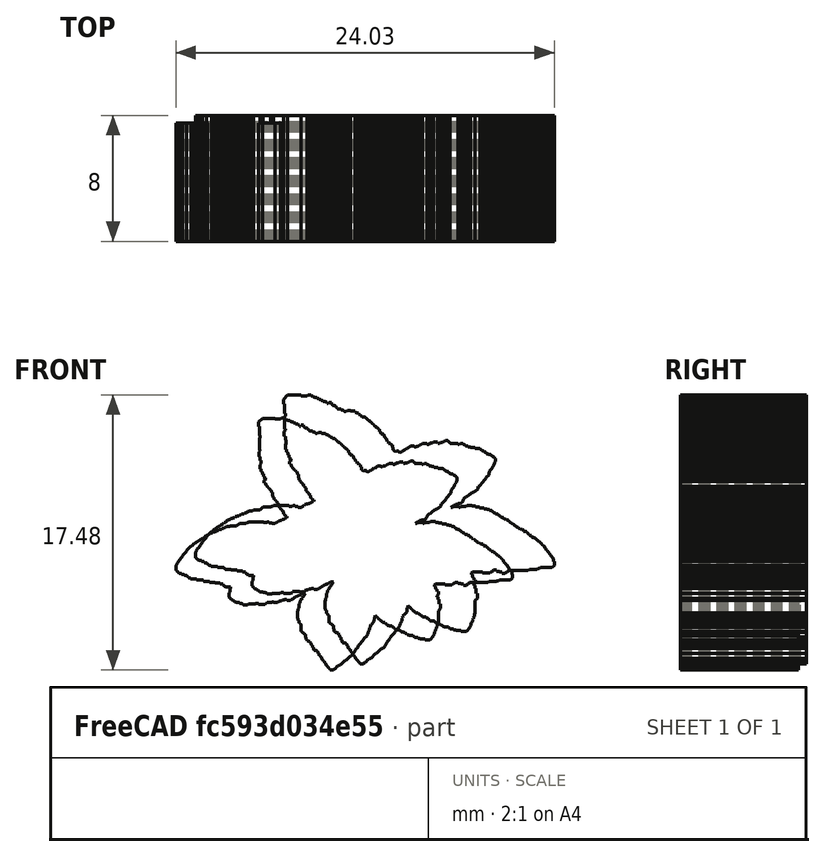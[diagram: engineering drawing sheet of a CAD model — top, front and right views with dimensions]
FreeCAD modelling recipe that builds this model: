
FCSTD DOCUMENT  (FreeCAD 0.20R29410 (Git))
Label: mintsLeafLogo_01_13_2023
License: All rights reserved
LicenseURL: http://en.wikipedia.org/wiki/All_rights_reserved
objects: Part::FeaturePython×2, Sketcher::SketchObject×1, Mesh::Feature×1, Part::Extrusion×1
note: 4 computed .brp shape members not serialized (recipe doc carries the construction recipe); baked Part::Feature solids carry a one-line shape summary decoded from their .brp

FEATURE [Sketcher::SketchObject] Sketch013
  FullyConstrained = false
  Placement = pos=(0,0,0) rot=(1,0,0;1.5708rad)
  sketch-geometry (884):
    g0: LineSegment StartX=35.7189 StartY=14.4677 StartZ=0 EndX=35.5415 EndY=14.2824 EndZ=0
    g1: LineSegment StartX=35.5415 StartY=14.2079 StartZ=0 EndX=35.4533 EndY=14.1342 EndZ=0
    g2: LineSegment StartX=35.4533 StartY=14.1342 StartZ=0 EndX=35.4583 EndY=14.0618 EndZ=0
    g3: LineSegment StartX=35.4583 StartY=14.0618 StartZ=0 EndX=35.3195 EndY=13.9216 EndZ=0
    g4: LineSegment StartX=35.3195 StartY=13.9216 StartZ=0 EndX=35.3195 EndY=13.853 EndZ=0
    g5: LineSegment StartX=35.3195 StartY=13.853 StartZ=0 EndX=35.248 EndY=13.7975 EndZ=0
    g6: LineSegment StartX=35.248 StartY=13.7975 StartZ=0 EndX=35.248 EndY=13.6573 EndZ=0
    g7: LineSegment StartX=35.248 StartY=13.6573 StartZ=0 EndX=35.1825 EndY=13.5912 EndZ=0
    g8: LineSegment StartX=35.1825 StartY=13.5912 StartZ=0 EndX=35.1825 EndY=13.2647 EndZ=0
    g9: LineSegment StartX=35.1825 StartY=13.2647 StartZ=0 EndX=35.0994 EndY=13.159 EndZ=0
    g10: LineSegment StartX=35.0994 StartY=13.159 StartZ=0 EndX=35.0994 EndY=13.0459 EndZ=0
    g11: LineSegment StartX=35.0994 StartY=13.0459 StartZ=0 EndX=35.0336 EndY=12.9565 EndZ=0
    g12: LineSegment StartX=35.0336 StartY=12.9565 StartZ=0 EndX=35.0336 EndY=12.3489 EndZ=0
    g13: LineSegment StartX=35.0336 StartY=12.3489 StartZ=0 EndX=35.1008 EndY=12.3489 EndZ=0
    g14: LineSegment StartX=35.1008 StartY=12.3489 StartZ=0 EndX=35.1008 EndY=12.2102 EndZ=0
    g15: LineSegment StartX=35.1008 StartY=12.2102 StartZ=0 EndX=35.1709 EndY=12.2072 EndZ=0
    g16: LineSegment StartX=35.1709 StartY=12.2072 StartZ=0 EndX=35.1709 EndY=11.9948 EndZ=0
    g17: LineSegment StartX=35.1709 StartY=11.9948 StartZ=0 EndX=35.2359 EndY=11.9948 EndZ=0
    g18: LineSegment StartX=35.2359 StartY=11.9948 StartZ=0 EndX=35.2359 EndY=11.9181 EndZ=0
    g19: LineSegment StartX=35.2359 StartY=11.9181 StartZ=0 EndX=35.3001 EndY=11.9181 EndZ=0
    g20: LineSegment StartX=35.3001 StartY=11.9181 StartZ=0 EndX=35.3001 EndY=11.8402 EndZ=0
    g21: LineSegment StartX=35.3001 StartY=11.8402 StartZ=0 EndX=35.3675 EndY=11.8402 EndZ=0
    g22: LineSegment StartX=35.3675 StartY=11.8402 StartZ=0 EndX=35.3675 EndY=11.2433 EndZ=0
    g23: LineSegment StartX=35.3675 StartY=11.2433 StartZ=0 EndX=35.435 EndY=11.2433 EndZ=0
    g24: LineSegment StartX=35.435 StartY=11.2433 StartZ=0 EndX=35.435 EndY=11.1727 EndZ=0
    g25: LineSegment StartX=35.435 StartY=11.1727 StartZ=0 EndX=35.5098 EndY=11.1727 EndZ=0
    g26: LineSegment StartX=35.5098 StartY=11.1727 StartZ=0 EndX=35.5098 EndY=11.1026 EndZ=0
    g27: LineSegment StartX=35.5098 StartY=11.1026 StartZ=0 EndX=35.6558 EndY=11.1026 EndZ=0
    g28: LineSegment StartX=35.6558 StartY=11.1026 StartZ=0 EndX=35.6558 EndY=11.0252 EndZ=0
    g29: LineSegment StartX=35.6558 StartY=11.0252 StartZ=0 EndX=35.7128 EndY=11.0252 EndZ=0
    g30: LineSegment StartX=35.7128 StartY=11.0252 StartZ=0 EndX=35.7128 EndY=10.7682 EndZ=0
    g31: LineSegment StartX=35.7128 StartY=10.7682 StartZ=0 EndX=35.7756 EndY=10.7681 EndZ=0
    g32: LineSegment StartX=35.7756 StartY=10.7681 StartZ=0 EndX=35.7756 EndY=10.5644 EndZ=0
    g33: LineSegment StartX=35.7756 StartY=10.5644 StartZ=0 EndX=35.846 EndY=10.5644 EndZ=0
    g34: LineSegment StartX=35.846 StartY=10.5644 StartZ=0 EndX=35.846 EndY=10.4767 EndZ=0
    g35: LineSegment StartX=35.846 StartY=10.4767 StartZ=0 EndX=35.988 EndY=10.4767 EndZ=0
    g36: LineSegment StartX=35.988 StartY=10.4767 StartZ=0 EndX=35.988 EndY=10.4228 EndZ=0
    g37: LineSegment StartX=35.988 StartY=10.4228 StartZ=0 EndX=36.1201 EndY=10.4228 EndZ=0
    g38: LineSegment StartX=36.1201 StartY=10.4228 StartZ=0 EndX=36.1201 EndY=10.2907 EndZ=0
    g39: LineSegment StartX=36.1201 StartY=10.2907 StartZ=0 EndX=36.1926 EndY=10.2907 EndZ=0
    g40: LineSegment StartX=36.1926 StartY=10.2907 StartZ=0 EndX=36.1926 EndY=10.1585 EndZ=0
    g41: LineSegment StartX=36.1926 StartY=10.1585 StartZ=0 EndX=36.2533 EndY=10.1585 EndZ=0
    g42: LineSegment StartX=36.2533 StartY=10.1585 StartZ=0 EndX=36.2533 EndY=10.0897 EndZ=0
    g43: LineSegment StartX=36.2533 StartY=10.0897 StartZ=0 EndX=36.3179 EndY=10.0897 EndZ=0
    g44: LineSegment StartX=36.3179 StartY=10.0897 StartZ=0 EndX=36.3179 EndY=9.8871 EndZ=0
    g45: LineSegment StartX=36.3179 StartY=9.8871 StartZ=0 EndX=36.3888 EndY=9.8871 EndZ=0
    g46: LineSegment StartX=36.3888 StartY=9.8871 StartZ=0 EndX=36.3888 EndY=9.73503 EndZ=0
    g47: LineSegment StartX=36.3888 StartY=9.73503 StartZ=0 EndX=36.4516 EndY=9.73503 EndZ=0
    g48: LineSegment StartX=36.4516 StartY=9.73503 StartZ=0 EndX=36.4516 EndY=9.65617 EndZ=0
    g49: LineSegment StartX=36.4516 StartY=9.65617 StartZ=0 EndX=36.6707 EndY=9.65617 EndZ=0
    g50: LineSegment StartX=36.6707 StartY=9.65617 StartZ=0 EndX=36.6707 EndY=9.58899 EndZ=0
    g51: LineSegment StartX=36.6707 StartY=9.58899 StartZ=0 EndX=36.7335 EndY=9.58899 EndZ=0
    g52: LineSegment StartX=36.7335 StartY=9.58899 StartZ=0 EndX=36.7335 EndY=9.51158 EndZ=0
    g53: LineSegment StartX=36.7335 StartY=9.51158 StartZ=0 EndX=36.7948 EndY=9.51158 EndZ=0
    g54: LineSegment StartX=36.7948 StartY=9.51158 StartZ=0 EndX=36.7948 EndY=9.40351 EndZ=0
    g55: LineSegment StartX=36.7948 StartY=9.40351 StartZ=0 EndX=36.8664 EndY=9.40351 EndZ=0
    g56: LineSegment StartX=36.8664 StartY=9.40351 StartZ=0 EndX=36.8664 EndY=9.2487 EndZ=0
    g57: LineSegment StartX=36.8664 StartY=9.2487 StartZ=0 EndX=36.9292 EndY=9.2487 EndZ=0
    g58: LineSegment StartX=36.9292 StartY=9.2487 StartZ=0 EndX=36.9292 EndY=9.18298 EndZ=0
    g59: LineSegment StartX=36.9292 StartY=9.18298 StartZ=0 EndX=37.0036 EndY=9.18298 EndZ=0
    g60: LineSegment StartX=37.0036 StartY=9.18298 StartZ=0 EndX=37.0036 EndY=9.12121 EndZ=0
    g61: LineSegment StartX=37.0036 StartY=9.12121 StartZ=0 EndX=37.066 EndY=9.12121 EndZ=0
    g62: LineSegment StartX=37.066 StartY=9.12121 StartZ=0 EndX=37.066 EndY=8.98122 EndZ=0
    g63: LineSegment StartX=37.066 StartY=8.98122 StartZ=0 EndX=37.1365 EndY=8.98122 EndZ=0
    g64: LineSegment StartX=37.1365 StartY=8.98122 StartZ=0 EndX=37.1365 EndY=8.85617 EndZ=0
    g65: LineSegment StartX=37.1365 StartY=8.85617 StartZ=0 EndX=37.2117 EndY=8.85617 EndZ=0
    g66: LineSegment StartX=37.2117 StartY=8.85617 StartZ=0 EndX=37.2117 EndY=8.77808 EndZ=0
    g67: LineSegment StartX=37.2117 StartY=8.77808 StartZ=0 EndX=37.276 EndY=8.7779 EndZ=0
    g68: LineSegment StartX=37.276 StartY=8.7779 StartZ=0 EndX=37.276 EndY=8.70839 EndZ=0
    g69: LineSegment StartX=37.276 StartY=8.70839 StartZ=0 EndX=37.3475 EndY=8.70839 EndZ=0
    g70: LineSegment StartX=37.3475 StartY=8.70839 StartZ=0 EndX=37.3475 EndY=8.58602 EndZ=0
    g71: LineSegment StartX=37.3475 StartY=8.58602 StartZ=0 EndX=37.4111 EndY=8.58602 EndZ=0
    g72: LineSegment StartX=37.4111 StartY=8.58602 StartZ=0 EndX=37.4111 EndY=8.50272 EndZ=0
    g73: LineSegment StartX=37.4111 StartY=8.50272 StartZ=0 EndX=37.4778 EndY=8.50272 EndZ=0
    g74: LineSegment StartX=37.4778 StartY=8.50272 StartZ=0 EndX=37.4778 EndY=8.37852 EndZ=0
    g75: LineSegment StartX=37.4778 StartY=8.37852 StartZ=0 EndX=37.55 EndY=8.37852 EndZ=0
    g76: LineSegment StartX=37.55 StartY=8.37852 StartZ=0 EndX=37.55 EndY=8.29594 EndZ=0
    g77: LineSegment StartX=37.55 StartY=8.29594 StartZ=0 EndX=37.6238 EndY=8.29594 EndZ=0
    g78: LineSegment StartX=37.6238 StartY=8.29594 StartZ=0 EndX=37.6238 EndY=8.20831 EndZ=0
    g79: LineSegment StartX=37.6238 StartY=8.20831 StartZ=0 EndX=37.6953 EndY=8.21123 EndZ=0
    g80: LineSegment StartX=37.6953 StartY=8.21123 StartZ=0 EndX=37.6953 EndY=8.14022 EndZ=0
    g81: LineSegment StartX=37.6953 StartY=8.14022 StartZ=0 EndX=37.7536 EndY=8.14414 EndZ=0
    g82: LineSegment StartX=37.7536 StartY=8.14414 StartZ=0 EndX=37.7574 EndY=8.06459 EndZ=0
    g83: LineSegment StartX=37.7574 StartY=8.06459 StartZ=0 EndX=37.8181 EndY=8.06459 EndZ=0
    g84: LineSegment StartX=37.8181 StartY=8.06459 StartZ=0 EndX=37.8216 EndY=7.98967 EndZ=0
    g85: LineSegment StartX=37.8216 StartY=7.98967 StartZ=0 EndX=38.1025 EndY=7.98967 EndZ=0
    g86: LineSegment StartX=38.1025 StartY=7.98967 StartZ=0 EndX=38.1917 EndY=8.08042 EndZ=0
    g87: LineSegment StartX=38.1917 StartY=8.08042 StartZ=0 EndX=38.2417 EndY=8.08577 EndZ=0
    g88: LineSegment StartX=38.2417 StartY=8.08577 StartZ=0 EndX=38.4557 EndY=8.32302 EndZ=0
    g89: LineSegment StartX=38.4557 StartY=8.32302 StartZ=0 EndX=38.5235 EndY=8.32302 EndZ=0
    g90: LineSegment StartX=38.5235 StartY=8.32302 StartZ=0 EndX=38.5887 EndY=8.40314 EndZ=0
    g91: LineSegment StartX=38.5887 StartY=8.40314 StartZ=0 EndX=38.6773 EndY=8.40314 EndZ=0
    g92: LineSegment StartX=38.6773 StartY=8.40314 StartZ=0 EndX=39.0643 EndY=8.80818 EndZ=0
    g93: LineSegment StartX=39.0643 StartY=8.80818 StartZ=0 EndX=39.152 EndY=8.80818 EndZ=0
    g94: LineSegment StartX=39.152 StartY=8.80818 StartZ=0 EndX=39.5355 EndY=9.19803 EndZ=0
    g95: LineSegment StartX=39.5355 StartY=9.19803 StartZ=0 EndX=39.6318 EndY=9.19803 EndZ=0
    g96: LineSegment StartX=39.6318 StartY=9.19803 StartZ=0 EndX=39.792 EndY=9.38195 EndZ=0
    g97: LineSegment StartX=39.792 StartY=9.38195 StartZ=0 EndX=39.7884 EndY=9.45608 EndZ=0
    g98: LineSegment StartX=39.7884 StartY=9.45608 StartZ=0 EndX=39.9772 EndY=9.63446 EndZ=0
    g99: LineSegment StartX=39.9772 StartY=9.63446 StartZ=0 EndX=39.9772 EndY=9.72533 EndZ=0
    g100: LineSegment StartX=39.9772 StartY=9.72533 StartZ=0 EndX=40.1697 EndY=9.91904 EndZ=0
    g101: LineSegment StartX=40.1697 StartY=9.91904 StartZ=0 EndX=40.1746 EndY=9.99558 EndZ=0
    g102: LineSegment StartX=40.1746 StartY=9.99558 StartZ=0 EndX=40.2388 EndY=10.0603 EndZ=0
    g103: LineSegment StartX=40.2388 StartY=10.0603 StartZ=0 EndX=40.2423 EndY=10.1261 EndZ=0
    g104: LineSegment StartX=40.2423 StartY=10.1261 StartZ=0 EndX=40.5948 EndY=10.4793 EndZ=0
    g105: LineSegment StartX=40.5948 StartY=10.4793 StartZ=0 EndX=40.5948 EndY=10.5499 EndZ=0
    g106: LineSegment StartX=40.5948 StartY=10.5499 StartZ=0 EndX=40.6701 EndY=10.618 EndZ=0
    g107: LineSegment StartX=40.6701 StartY=10.618 StartZ=0 EndX=40.6581 EndY=10.6527 EndZ=0
    g108: LineSegment StartX=40.6581 StartY=10.6527 StartZ=0 EndX=40.6988 EndY=10.6527 EndZ=0
    g109: LineSegment StartX=40.6988 StartY=10.6527 StartZ=0 EndX=40.9317 EndY=10.8877 EndZ=0
    g110: LineSegment StartX=40.9317 StartY=10.8877 StartZ=0 EndX=40.9317 EndY=10.9592 EndZ=0
    g111: LineSegment StartX=40.9317 StartY=10.9592 StartZ=0 EndX=41.0136 EndY=11.0405 EndZ=0
    g112: LineSegment StartX=41.0136 StartY=11.0405 StartZ=0 EndX=41.0068 EndY=11.1648 EndZ=0
    g113: LineSegment StartX=41.0068 StartY=11.1648 StartZ=0 EndX=41.0763 EndY=11.2275 EndZ=0
    g114: LineSegment StartX=41.0763 StartY=11.2275 StartZ=0 EndX=41.0723 EndY=11.2979 EndZ=0
    g115: LineSegment StartX=41.0723 StartY=11.2979 StartZ=0 EndX=41.15 EndY=11.3821 EndZ=0
    g116: LineSegment StartX=41.15 StartY=11.3821 StartZ=0 EndX=41.15 EndY=11.5724 EndZ=0
    g117: LineSegment StartX=41.15 StartY=11.5724 StartZ=0 EndX=41.2317 EndY=11.6351 EndZ=0
    g118: LineSegment StartX=41.2317 StartY=11.6351 StartZ=0 EndX=41.2155 EndY=11.7717 EndZ=0
    g119: LineSegment StartX=41.2155 StartY=11.7717 StartZ=0 EndX=41.2837 EndY=11.8432 EndZ=0
    g120: LineSegment StartX=41.2837 StartY=11.8432 StartZ=0 EndX=41.2786 EndY=11.8698 EndZ=0
    g121: LineSegment StartX=41.2786 StartY=11.8698 StartZ=0 EndX=41.3138 EndY=11.8698 EndZ=0
    g122: LineSegment StartX=41.3138 StartY=11.8698 StartZ=0 EndX=41.5455 EndY=12.1045 EndZ=0
    g123: LineSegment StartX=41.5455 StartY=12.1045 StartZ=0 EndX=41.5618 EndY=12.4305 EndZ=0
    g124: LineSegment StartX=41.5618 StartY=12.4305 StartZ=0 EndX=41.6277 EndY=12.505 EndZ=0
    g125: LineSegment StartX=41.6277 StartY=12.505 StartZ=0 EndX=41.6277 EndY=12.6108 EndZ=0
    g126: LineSegment StartX=41.6277 StartY=12.6108 StartZ=0 EndX=41.692 EndY=12.5393 EndZ=0
    g127: LineSegment StartX=41.692 StartY=12.5393 StartZ=0 EndX=41.7679 EndY=12.5393 EndZ=0
    g128: LineSegment StartX=41.7679 StartY=12.5393 StartZ=0 EndX=41.7679 EndY=12.4516 EndZ=0
    g129: LineSegment StartX=41.7679 StartY=12.4516 StartZ=0 EndX=41.8336 EndY=12.4546 EndZ=0
    g130: LineSegment StartX=41.8336 StartY=12.4546 StartZ=0 EndX=41.8336 EndY=12.3903 EndZ=0
    g131: LineSegment StartX=41.8336 StartY=12.3903 StartZ=0 EndX=41.8935 EndY=12.3903 EndZ=0
    g132: LineSegment StartX=41.8935 StartY=12.3903 StartZ=0 EndX=41.8935 EndY=12.3173 EndZ=0
    g133: LineSegment StartX=41.8935 StartY=12.3173 StartZ=0 EndX=41.9592 EndY=12.3217 EndZ=0
    g134: LineSegment StartX=41.9592 StartY=12.3217 StartZ=0 EndX=41.9651 EndY=12.2501 EndZ=0
    g135: LineSegment StartX=41.9651 StartY=12.2501 StartZ=0 EndX=42.0235 EndY=12.2559 EndZ=0
    g136: LineSegment StartX=42.0235 StartY=12.2559 StartZ=0 EndX=42.0264 EndY=12.1829 EndZ=0
    g137: LineSegment StartX=42.0264 StartY=12.1829 StartZ=0 EndX=42.1067 EndY=12.1888 EndZ=0
    g138: LineSegment StartX=42.1067 StartY=12.1888 StartZ=0 EndX=42.1067 EndY=12.1143 EndZ=0
    g139: LineSegment StartX=42.1067 StartY=12.1143 StartZ=0 EndX=42.2426 EndY=12.1216 EndZ=0
    g140: LineSegment StartX=42.2426 StartY=12.1216 StartZ=0 EndX=42.2426 EndY=12.0413 EndZ=0
    g141: LineSegment StartX=42.2426 StartY=12.0413 StartZ=0 EndX=42.4427 EndY=12.0413 EndZ=0
    g142: LineSegment StartX=42.4427 StartY=12.0413 StartZ=0 EndX=42.45 EndY=11.9566 EndZ=0
    g143: LineSegment StartX=42.45 StartY=11.9566 StartZ=0 EndX=42.523 EndY=11.9639 EndZ=0
    g144: LineSegment StartX=42.523 StartY=11.9639 StartZ=0 EndX=42.5274 EndY=11.8952 EndZ=0
    g145: LineSegment StartX=42.5274 StartY=11.8952 StartZ=0 EndX=42.5931 EndY=11.9011 EndZ=0
    g146: LineSegment StartX=42.5931 StartY=11.9011 StartZ=0 EndX=42.5931 EndY=11.847 EndZ=0
    g147: LineSegment StartX=42.5931 StartY=11.847 StartZ=0 EndX=42.6457 EndY=11.8499 EndZ=0
    g148: LineSegment StartX=42.6457 StartY=11.8499 StartZ=0 EndX=42.6457 EndY=11.7886 EndZ=0
    g149: LineSegment StartX=42.6457 StartY=11.7886 StartZ=0 EndX=42.7844 EndY=11.7886 EndZ=0
    g150: LineSegment StartX=42.7844 StartY=11.7886 StartZ=0 EndX=42.7844 EndY=11.7131 EndZ=0
    g151: LineSegment StartX=42.7844 StartY=11.7131 StartZ=0 EndX=43.0642 EndY=11.7131 EndZ=0
    g152: LineSegment StartX=43.0642 StartY=11.7131 StartZ=0 EndX=43.0642 EndY=11.6357 EndZ=0
    g153: LineSegment StartX=43.0642 StartY=11.6357 StartZ=0 EndX=43.1985 EndY=11.6357 EndZ=0
    g154: LineSegment StartX=43.1985 StartY=11.6357 StartZ=0 EndX=43.1985 EndY=11.5714 EndZ=0
    g155: LineSegment StartX=43.1985 StartY=11.5714 StartZ=0 EndX=43.2613 EndY=11.5714 EndZ=0
    g156: LineSegment StartX=43.2613 StartY=11.5714 StartZ=0 EndX=43.2613 EndY=11.5086 EndZ=0
    g157: LineSegment StartX=43.2613 StartY=11.5086 StartZ=0 EndX=43.3285 EndY=11.5086 EndZ=0
    g158: LineSegment StartX=43.3285 StartY=11.5086 StartZ=0 EndX=43.3285 EndY=11.4327 EndZ=0
    g159: LineSegment StartX=43.3285 StartY=11.4327 StartZ=0 EndX=43.3913 EndY=11.4371 EndZ=0
    g160: LineSegment StartX=43.3913 StartY=11.4371 StartZ=0 EndX=43.3932 EndY=11.3717 EndZ=0
    g161: LineSegment StartX=43.3932 StartY=11.3717 StartZ=0 EndX=43.7436 EndY=11.3717 EndZ=0
    g162: LineSegment StartX=43.7436 StartY=11.3717 StartZ=0 EndX=43.7436 EndY=11.3021 EndZ=0
    g163: LineSegment StartX=43.7436 StartY=11.3021 StartZ=0 EndX=43.8098 EndY=11.3021 EndZ=0
    g164: LineSegment StartX=43.8098 StartY=11.3021 StartZ=0 EndX=43.8134 EndY=11.2285 EndZ=0
    g165: LineSegment StartX=43.8134 StartY=11.2285 StartZ=0 EndX=44.0238 EndY=11.2285 EndZ=0
    g166: LineSegment StartX=44.0238 StartY=11.2285 StartZ=0 EndX=44.0238 EndY=11.1603 EndZ=0
    g167: LineSegment StartX=44.0238 StartY=11.1603 StartZ=0 EndX=44.1542 EndY=11.1603 EndZ=0
    g168: LineSegment StartX=44.1542 StartY=11.1603 StartZ=0 EndX=44.1506 EndY=11.0922 EndZ=0
    g169: LineSegment StartX=44.1506 StartY=11.0922 StartZ=0 EndX=44.2845 EndY=11.1005 EndZ=0
    g170: LineSegment StartX=44.2845 StartY=11.1005 StartZ=0 EndX=44.2845 EndY=11.0276 EndZ=0
    g171: LineSegment StartX=44.2845 StartY=11.0276 StartZ=0 EndX=44.3538 EndY=11.0312 EndZ=0
    g172: LineSegment StartX=44.3538 StartY=11.0312 StartZ=0 EndX=44.3538 EndY=10.9534 EndZ=0
    g173: LineSegment StartX=44.3538 StartY=10.9534 StartZ=0 EndX=44.4925 EndY=10.9534 EndZ=0
    g174: LineSegment StartX=44.4925 StartY=10.9534 StartZ=0 EndX=44.4925 EndY=10.9066 EndZ=0
    g175: LineSegment StartX=44.4925 StartY=10.9066 StartZ=0 EndX=44.8405 EndY=10.9066 EndZ=0
    g176: LineSegment StartX=44.8405 StartY=10.9066 StartZ=0 EndX=44.8405 EndY=10.8227 EndZ=0
    g177: LineSegment StartX=44.8405 StartY=10.8227 StartZ=0 EndX=44.9671 EndY=10.8245 EndZ=0
    g178: LineSegment StartX=44.9671 StartY=10.8245 StartZ=0 EndX=44.9671 EndY=10.7496 EndZ=0
    g179: LineSegment StartX=44.9671 StartY=10.7496 StartZ=0 EndX=45.2382 EndY=10.7496 EndZ=0
    g180: LineSegment StartX=45.2382 StartY=10.7496 StartZ=0 EndX=45.2382 EndY=10.6783 EndZ=0
    g181: LineSegment StartX=45.2382 StartY=10.6783 StartZ=0 EndX=45.438 EndY=10.6783 EndZ=0
    g182: LineSegment StartX=45.438 StartY=10.6783 StartZ=0 EndX=45.438 EndY=10.6176 EndZ=0
    g183: LineSegment StartX=45.438 StartY=10.6176 StartZ=0 EndX=45.8572 EndY=10.6176 EndZ=0
    g184: LineSegment StartX=45.8572 StartY=10.6176 StartZ=0 EndX=45.8572 EndY=10.548 EndZ=0
    g185: LineSegment StartX=45.8572 StartY=10.548 StartZ=0 EndX=46.2711 EndY=10.548 EndZ=0
    g186: LineSegment StartX=46.2711 StartY=10.548 StartZ=0 EndX=46.5712 EndY=10.876 EndZ=0
    g187: LineSegment StartX=46.5712 StartY=10.876 StartZ=0 EndX=46.568 EndY=10.9537 EndZ=0
    g188: LineSegment StartX=46.568 StartY=10.9537 StartZ=0 EndX=46.6513 EndY=11.0387 EndZ=0
    g189: LineSegment StartX=46.6513 StartY=11.0387 StartZ=0 EndX=46.6513 EndY=11.2162 EndZ=0
    g190: LineSegment StartX=46.6513 StartY=11.2162 StartZ=0 EndX=46.7535 EndY=11.317 EndZ=0
    g191: LineSegment StartX=46.7535 StartY=11.317 StartZ=0 EndX=46.7462 EndY=11.4353 EndZ=0
    g192: LineSegment StartX=46.7462 StartY=11.4353 StartZ=0 EndX=46.8178 EndY=11.5141 EndZ=0
    g193: LineSegment StartX=46.8178 StartY=11.5141 StartZ=0 EndX=46.8081 EndY=11.636 EndZ=0
    g194: LineSegment StartX=46.8081 StartY=11.636 StartZ=0 EndX=46.8919 EndY=11.7287 EndZ=0
    g195: LineSegment StartX=46.8919 StartY=11.7287 StartZ=0 EndX=46.8919 EndY=11.9142 EndZ=0
    g196: LineSegment StartX=46.8919 StartY=11.9142 StartZ=0 EndX=46.9704 EndY=12.0106 EndZ=0
    g197: LineSegment StartX=46.9704 StartY=12.0106 StartZ=0 EndX=46.9704 EndY=13.0147 EndZ=0
    g198: LineSegment StartX=46.9704 StartY=13.0147 StartZ=0 EndX=47.1435 EndY=13.1957 EndZ=0
    g199: LineSegment StartX=47.1435 StartY=13.1957 StartZ=0 EndX=47.1435 EndY=13.5812 EndZ=0
    g200: LineSegment StartX=47.1435 StartY=13.5812 StartZ=0 EndX=47.0232 EndY=13.5812 EndZ=0
    g201: LineSegment StartX=47.0232 StartY=13.5812 StartZ=0 EndX=47.0232 EndY=13.968 EndZ=0
    g202: LineSegment StartX=47.0232 StartY=13.968 StartZ=0 EndX=46.9387 EndY=13.981 EndZ=0
    g203: LineSegment StartX=46.9387 StartY=13.981 StartZ=0 EndX=46.9387 EndY=14.1923 EndZ=0
    g204: LineSegment StartX=46.9387 StartY=14.1923 StartZ=0 EndX=46.8607 EndY=14.189 EndZ=0
    g205: LineSegment StartX=46.8607 StartY=14.189 StartZ=0 EndX=46.8607 EndY=14.2768 EndZ=0
    g206: LineSegment StartX=46.8607 StartY=14.2768 StartZ=0 EndX=46.9745 EndY=14.4003 EndZ=0
    g207: LineSegment StartX=46.9745 StartY=14.4003 StartZ=0 EndX=46.9842 EndY=14.6473 EndZ=0
    g208: LineSegment StartX=46.9842 StartY=14.6473 StartZ=0 EndX=46.8672 EndY=14.6603 EndZ=0
    g209: LineSegment StartX=46.8672 StartY=14.6603 StartZ=0 EndX=46.8672 EndY=14.8066 EndZ=0
    g210: LineSegment StartX=46.8672 StartY=14.8066 StartZ=0 EndX=46.799 EndY=14.8131 EndZ=0
    g211: LineSegment StartX=46.799 StartY=14.8131 StartZ=0 EndX=46.7957 EndY=14.8846 EndZ=0
    g212: LineSegment StartX=46.7957 StartY=14.8846 StartZ=0 EndX=46.7372 EndY=14.8911 EndZ=0
    g213: LineSegment StartX=46.7372 StartY=14.8911 StartZ=0 EndX=46.7502 EndY=15.0699 EndZ=0
    g214: LineSegment StartX=46.7502 StartY=15.0699 StartZ=0 EndX=46.6592 EndY=15.0764 EndZ=0
    g215: LineSegment StartX=46.6592 StartY=15.0764 StartZ=0 EndX=46.6592 EndY=15.2096 EndZ=0
    g216: LineSegment StartX=46.6592 StartY=15.2096 StartZ=0 EndX=46.7535 EndY=15.2811 EndZ=0
    g217: LineSegment StartX=46.7535 StartY=15.2811 StartZ=0 EndX=47.5498 EndY=15.2811 EndZ=0
    g218: LineSegment StartX=47.5498 StartY=15.2811 StartZ=0 EndX=47.5498 EndY=15.2015 EndZ=0
    g219: LineSegment StartX=47.5498 StartY=15.2015 StartZ=0 EndX=48.1326 EndY=15.2015 EndZ=0
    g220: LineSegment StartX=48.1326 StartY=15.2015 StartZ=0 EndX=48.1915 EndY=15.2887 EndZ=0
    g221: LineSegment StartX=48.1915 StartY=15.2887 StartZ=0 EndX=48.2811 EndY=15.2887 EndZ=0
    g222: LineSegment StartX=48.2811 StartY=15.2887 StartZ=0 EndX=48.4046 EndY=15.4194 EndZ=0
    g223: LineSegment StartX=48.4046 StartY=15.4194 StartZ=0 EndX=48.6512 EndY=15.4194 EndZ=0
    g224: LineSegment StartX=48.6512 StartY=15.4194 StartZ=0 EndX=48.6512 EndY=15.3322 EndZ=0
    g225: LineSegment StartX=48.6512 StartY=15.3322 StartZ=0 EndX=48.9084 EndY=15.3322 EndZ=0
    g226: LineSegment StartX=48.9084 StartY=15.3322 StartZ=0 EndX=48.9084 EndY=15.2647 EndZ=0
    g227: LineSegment StartX=48.9084 StartY=15.2647 StartZ=0 EndX=49.1131 EndY=15.2647 EndZ=0
    g228: LineSegment StartX=49.1131 StartY=15.2647 StartZ=0 EndX=49.1131 EndY=15.171 EndZ=0
    g229: LineSegment StartX=49.1131 StartY=15.171 StartZ=0 EndX=49.344 EndY=15.171 EndZ=0
    g230: LineSegment StartX=49.344 StartY=15.171 StartZ=0 EndX=49.4317 EndY=15.2779 EndZ=0
    g231: LineSegment StartX=49.4317 StartY=15.2779 StartZ=0 EndX=49.513 EndY=15.2714 EndZ=0
    g232: LineSegment StartX=49.513 StartY=15.2714 StartZ=0 EndX=49.6365 EndY=15.4177 EndZ=0
    g233: LineSegment StartX=49.6365 StartY=15.4177 StartZ=0 EndX=51.1609 EndY=15.4177 EndZ=0
    g234: LineSegment StartX=51.1609 StartY=15.4177 StartZ=0 EndX=51.2713 EndY=15.4747 EndZ=0
    g235: LineSegment StartX=51.2713 StartY=15.4747 StartZ=0 EndX=51.8707 EndY=15.4747 EndZ=0
    g236: LineSegment StartX=51.8707 StartY=15.4747 StartZ=0 EndX=51.9501 EndY=15.5501 EndZ=0
    g237: LineSegment StartX=51.9501 StartY=15.5501 StartZ=0 EndX=52.0613 EndY=15.5501 EndZ=0
    g238: LineSegment StartX=52.0613 StartY=15.5501 StartZ=0 EndX=52.1566 EndY=15.6335 EndZ=0
    g239: LineSegment StartX=52.1566 StartY=15.6335 StartZ=0 EndX=53.0776 EndY=15.6335 EndZ=0
    g240: LineSegment StartX=53.0776 StartY=15.6335 StartZ=0 EndX=53.2557 EndY=15.8082 EndZ=0
    g241: LineSegment StartX=53.2557 StartY=15.8082 StartZ=0 EndX=53.2557 EndY=16.103 EndZ=0
    g242: LineSegment StartX=53.2557 StartY=16.103 StartZ=0 EndX=53.1958 EndY=16.103 EndZ=0
    g243: LineSegment StartX=53.1958 StartY=16.103 StartZ=0 EndX=53.1958 EndY=16.3046 EndZ=0
    g244: LineSegment StartX=53.1958 StartY=16.3046 StartZ=0 EndX=53.1301 EndY=16.3017 EndZ=0
    g245: LineSegment StartX=53.1301 StartY=16.3017 StartZ=0 EndX=53.1301 EndY=16.4404 EndZ=0
    g246: LineSegment StartX=53.1301 StartY=16.4404 StartZ=0 EndX=53.0594 EndY=16.4404 EndZ=0
    g247: LineSegment StartX=53.0594 StartY=16.4404 StartZ=0 EndX=53.0558 EndY=16.5171 EndZ=0
    g248: LineSegment StartX=53.0558 StartY=16.5171 StartZ=0 EndX=52.9773 EndY=16.5171 EndZ=0
    g249: LineSegment StartX=52.9773 StartY=16.5171 StartZ=0 EndX=52.9773 EndY=16.6455 EndZ=0
    g250: LineSegment StartX=52.9773 StartY=16.6455 StartZ=0 EndX=52.9219 EndY=16.6452 EndZ=0
    g251: LineSegment StartX=52.9219 StartY=16.6452 StartZ=0 EndX=52.9219 EndY=16.7146 EndZ=0
    g252: LineSegment StartX=52.9219 StartY=16.7146 StartZ=0 EndX=52.8549 EndY=16.7146 EndZ=0
    g253: LineSegment StartX=52.8549 StartY=16.7146 StartZ=0 EndX=52.8535 EndY=16.7863 EndZ=0
    g254: LineSegment StartX=52.8535 StartY=16.7863 StartZ=0 EndX=52.7868 EndY=16.7863 EndZ=0
    g255: LineSegment StartX=52.7868 StartY=16.7863 StartZ=0 EndX=52.7868 EndY=16.9211 EndZ=0
    g256: LineSegment StartX=52.7868 StartY=16.9211 StartZ=0 EndX=52.715 EndY=16.9211 EndZ=0
    g257: LineSegment StartX=52.715 StartY=16.9211 StartZ=0 EndX=52.715 EndY=16.98 EndZ=0
    g258: LineSegment StartX=52.715 StartY=16.98 StartZ=0 EndX=52.6457 EndY=16.98 EndZ=0
    g259: LineSegment StartX=52.6457 StartY=16.98 StartZ=0 EndX=52.6457 EndY=17.0366 EndZ=0
    g260: LineSegment StartX=52.6457 StartY=17.0366 StartZ=0 EndX=52.5763 EndY=17.0366 EndZ=0
    g261: LineSegment StartX=52.5763 StartY=17.0366 StartZ=0 EndX=52.5763 EndY=17.128 EndZ=0
    g262: LineSegment StartX=52.5763 StartY=17.128 StartZ=0 EndX=52.5147 EndY=17.128 EndZ=0
    g263: LineSegment StartX=52.5147 StartY=17.128 StartZ=0 EndX=52.5147 EndY=17.2695 EndZ=0
    g264: LineSegment StartX=52.5147 StartY=17.2695 StartZ=0 EndX=52.4502 EndY=17.2647 EndZ=0
    g265: LineSegment StartX=52.4502 StartY=17.2647 StartZ=0 EndX=52.4454 EndY=17.336 EndZ=0
    g266: LineSegment StartX=52.4454 StartY=17.336 StartZ=0 EndX=52.3797 EndY=17.3384 EndZ=0
    g267: LineSegment StartX=52.3797 StartY=17.3384 StartZ=0 EndX=52.3829 EndY=17.4058 EndZ=0
    g268: LineSegment StartX=52.3829 StartY=17.4058 StartZ=0 EndX=52.318 EndY=17.4026 EndZ=0
    g269: LineSegment StartX=52.318 StartY=17.4026 StartZ=0 EndX=52.318 EndY=17.4715 EndZ=0
    g270: LineSegment StartX=52.318 StartY=17.4715 StartZ=0 EndX=52.2451 EndY=17.4715 EndZ=0
    g271: LineSegment StartX=52.2451 StartY=17.4715 StartZ=0 EndX=52.2451 EndY=17.5364 EndZ=0
    g272: LineSegment StartX=52.2451 StartY=17.5364 StartZ=0 EndX=52.1833 EndY=17.5388 EndZ=0
    g273: LineSegment StartX=52.1833 StartY=17.5388 StartZ=0 EndX=52.1833 EndY=17.6077 EndZ=0
    g274: LineSegment StartX=52.1833 StartY=17.6077 StartZ=0 EndX=52.1144 EndY=17.6077 EndZ=0
    g275: LineSegment StartX=52.1144 StartY=17.6077 StartZ=0 EndX=52.1144 EndY=17.6741 EndZ=0
    g276: LineSegment StartX=52.1144 StartY=17.6741 StartZ=0 EndX=52.0495 EndY=17.6741 EndZ=0
    g277: LineSegment StartX=52.0495 StartY=17.6741 StartZ=0 EndX=52.0495 EndY=17.7495 EndZ=0
    g278: LineSegment StartX=52.0495 StartY=17.7495 StartZ=0 EndX=51.9017 EndY=17.7495 EndZ=0
    g279: LineSegment StartX=51.9017 StartY=17.7495 StartZ=0 EndX=51.9017 EndY=17.8092 EndZ=0
    g280: LineSegment StartX=51.9017 StartY=17.8092 StartZ=0 EndX=51.8351 EndY=17.8092 EndZ=0
    g281: LineSegment StartX=51.8351 StartY=17.8092 StartZ=0 EndX=51.8351 EndY=17.8911 EndZ=0
    g282: LineSegment StartX=51.8351 StartY=17.8911 StartZ=0 EndX=51.7639 EndY=17.8911 EndZ=0
    g283: LineSegment StartX=51.7639 StartY=17.8911 StartZ=0 EndX=51.7639 EndY=17.9626 EndZ=0
    g284: LineSegment StartX=51.7639 StartY=17.9626 StartZ=0 EndX=51.6325 EndY=17.9626 EndZ=0
    g285: LineSegment StartX=51.6325 StartY=17.9626 StartZ=0 EndX=51.6325 EndY=18.0284 EndZ=0
    g286: LineSegment StartX=51.6325 StartY=18.0284 StartZ=0 EndX=51.485 EndY=18.0284 EndZ=0
    g287: LineSegment StartX=51.485 StartY=18.0284 StartZ=0 EndX=51.485 EndY=18.0711 EndZ=0
    g288: LineSegment StartX=51.485 StartY=18.0711 StartZ=0 EndX=51.4163 EndY=18.0711 EndZ=0
    g289: LineSegment StartX=51.4163 StartY=18.0711 StartZ=0 EndX=51.4163 EndY=18.1587 EndZ=0
    g290: LineSegment StartX=51.4163 StartY=18.1587 StartZ=0 EndX=51.2878 EndY=18.1587 EndZ=0
    g291: LineSegment StartX=51.2878 StartY=18.1587 StartZ=0 EndX=51.2878 EndY=18.2275 EndZ=0
    g292: LineSegment StartX=51.2878 StartY=18.2275 StartZ=0 EndX=51.2232 EndY=18.2275 EndZ=0
    g293: LineSegment StartX=51.2232 StartY=18.2275 StartZ=0 EndX=51.2267 EndY=18.2921 EndZ=0
    g294: LineSegment StartX=51.2267 StartY=18.2921 StartZ=0 EndX=51.1526 EndY=18.2921 EndZ=0
    g295: LineSegment StartX=51.1526 StartY=18.2921 StartZ=0 EndX=51.1526 EndY=18.3662 EndZ=0
    g296: LineSegment StartX=51.1526 StartY=18.3662 StartZ=0 EndX=51.0845 EndY=18.3602 EndZ=0
    g297: LineSegment StartX=51.0845 StartY=18.3602 StartZ=0 EndX=51.0845 EndY=18.4424 EndZ=0
    g298: LineSegment StartX=51.0845 StartY=18.4424 StartZ=0 EndX=51.0222 EndY=18.4424 EndZ=0
    g299: LineSegment StartX=51.0222 StartY=18.4424 StartZ=0 EndX=51.0222 EndY=18.5138 EndZ=0
    g300: LineSegment StartX=51.0222 StartY=18.5138 StartZ=0 EndX=50.8169 EndY=18.5138 EndZ=0
    g301: LineSegment StartX=50.8169 StartY=18.5138 StartZ=0 EndX=50.7878 EndY=18.6026 EndZ=0
    g302: LineSegment StartX=50.7878 StartY=18.6026 StartZ=0 EndX=50.7494 EndY=18.6113 EndZ=0
    g303: LineSegment StartX=50.7494 StartY=18.6113 StartZ=0 EndX=50.7397 EndY=18.6731 EndZ=0
    g304: LineSegment StartX=50.7397 StartY=18.6731 StartZ=0 EndX=50.5414 EndY=18.6536 EndZ=0
    g305: LineSegment StartX=50.5414 StartY=18.6536 StartZ=0 EndX=50.5381 EndY=18.7381 EndZ=0
    g306: LineSegment StartX=50.5381 StartY=18.7381 StartZ=0 EndX=50.4114 EndY=18.7218 EndZ=0
    g307: LineSegment StartX=50.4114 StartY=18.7218 StartZ=0 EndX=50.3951 EndY=18.7934 EndZ=0
    g308: LineSegment StartX=50.3951 StartY=18.7934 StartZ=0 EndX=50.3334 EndY=18.7934 EndZ=0
    g309: LineSegment StartX=50.3334 StartY=18.7934 StartZ=0 EndX=50.3366 EndY=18.8389 EndZ=0
    g310: LineSegment StartX=50.3366 StartY=18.8389 StartZ=0 EndX=50.2066 EndY=18.8389 EndZ=0
    g311: LineSegment StartX=50.2066 StartY=18.8389 StartZ=0 EndX=50.2099 EndY=18.9201 EndZ=0
    g312: LineSegment StartX=50.2099 StartY=18.9201 StartZ=0 EndX=50.1254 EndY=18.9266 EndZ=0
    g313: LineSegment StartX=50.1254 StartY=18.9266 StartZ=0 EndX=50.1156 EndY=19.0046 EndZ=0
    g314: LineSegment StartX=50.1156 StartY=19.0046 StartZ=0 EndX=49.9986 EndY=18.9949 EndZ=0
    g315: LineSegment StartX=49.9986 StartY=18.9949 StartZ=0 EndX=49.9921 EndY=19.0859 EndZ=0
    g316: LineSegment StartX=49.9921 StartY=19.0859 StartZ=0 EndX=49.9368 EndY=19.0501 EndZ=0
    g317: LineSegment StartX=49.9368 StartY=19.0501 StartZ=0 EndX=49.9206 EndY=19.1509 EndZ=0
    g318: LineSegment StartX=49.9206 StartY=19.1509 StartZ=0 EndX=49.7971 EndY=19.1281 EndZ=0
    g319: LineSegment StartX=49.7971 StartY=19.1281 StartZ=0 EndX=49.8068 EndY=19.2029 EndZ=0
    g320: LineSegment StartX=49.8068 StartY=19.2029 StartZ=0 EndX=49.7288 EndY=19.1899 EndZ=0
    g321: LineSegment StartX=49.7288 StartY=19.1899 StartZ=0 EndX=49.7191 EndY=19.2582 EndZ=0
    g322: LineSegment StartX=49.7191 StartY=19.2582 StartZ=0 EndX=49.6606 EndY=19.2647 EndZ=0
    g323: LineSegment StartX=49.6606 StartY=19.2647 StartZ=0 EndX=49.6541 EndY=19.3329 EndZ=0
    g324: LineSegment StartX=49.6541 StartY=19.3329 StartZ=0 EndX=49.6021 EndY=19.3329 EndZ=0
    g325: LineSegment StartX=49.6021 StartY=19.3329 StartZ=0 EndX=49.5988 EndY=19.4077 EndZ=0
    g326: LineSegment StartX=49.5988 StartY=19.4077 StartZ=0 EndX=49.4623 EndY=19.3947 EndZ=0
    g327: LineSegment StartX=49.4623 StartY=19.3947 StartZ=0 EndX=49.4623 EndY=19.4727 EndZ=0
    g328: LineSegment StartX=49.4623 StartY=19.4727 StartZ=0 EndX=49.2543 EndY=19.4532 EndZ=0
    g329: LineSegment StartX=49.2543 StartY=19.4532 StartZ=0 EndX=49.2543 EndY=19.5279 EndZ=0
    g330: LineSegment StartX=49.2543 StartY=19.5279 StartZ=0 EndX=49.199 EndY=19.5279 EndZ=0
    g331: LineSegment StartX=49.199 StartY=19.5279 StartZ=0 EndX=49.199 EndY=19.6189 EndZ=0
    g332: LineSegment StartX=49.199 StartY=19.6189 StartZ=0 EndX=49.0658 EndY=19.6059 EndZ=0
    g333: LineSegment StartX=49.0658 StartY=19.6059 StartZ=0 EndX=49.0495 EndY=19.6612 EndZ=0
    g334: LineSegment StartX=49.0495 StartY=19.6612 StartZ=0 EndX=48.991 EndY=19.6547 EndZ=0
    g335: LineSegment StartX=48.991 StartY=19.6547 StartZ=0 EndX=48.9845 EndY=19.7359 EndZ=0
    g336: LineSegment StartX=48.9845 StartY=19.7359 StartZ=0 EndX=48.8577 EndY=19.7262 EndZ=0
    g337: LineSegment StartX=48.8577 StartY=19.7262 StartZ=0 EndX=48.8577 EndY=19.8149 EndZ=0
    g338: LineSegment StartX=48.8577 StartY=19.8149 StartZ=0 EndX=48.7743 EndY=19.8069 EndZ=0
    g339: LineSegment StartX=48.7743 StartY=19.8069 StartZ=0 EndX=48.7743 EndY=19.8894 EndZ=0
    g340: LineSegment StartX=48.7743 StartY=19.8894 StartZ=0 EndX=48.5854 EndY=19.8894 EndZ=0
    g341: LineSegment StartX=48.5854 StartY=19.8894 StartZ=0 EndX=48.5854 EndY=19.9533 EndZ=0
    g342: LineSegment StartX=48.5854 StartY=19.9533 StartZ=0 EndX=48.4417 EndY=19.9533 EndZ=0
    g343: LineSegment StartX=48.4417 StartY=19.9533 StartZ=0 EndX=48.4417 EndY=20.0118 EndZ=0
    g344: LineSegment StartX=48.4417 StartY=20.0118 StartZ=0 EndX=48.3751 EndY=20.0118 EndZ=0
    g345: LineSegment StartX=48.3751 StartY=20.0118 StartZ=0 EndX=48.3751 EndY=20.089 EndZ=0
    g346: LineSegment StartX=48.3751 StartY=20.089 StartZ=0 EndX=48.3033 EndY=20.089 EndZ=0
    g347: LineSegment StartX=48.3033 StartY=20.089 StartZ=0 EndX=48.3033 EndY=20.1524 EndZ=0
    g348: LineSegment StartX=48.3033 StartY=20.1524 StartZ=0 EndX=48.0916 EndY=20.1524 EndZ=0
    g349: LineSegment StartX=48.0916 StartY=20.1524 StartZ=0 EndX=48.0916 EndY=20.2331 EndZ=0
    g350: LineSegment StartX=48.0916 StartY=20.2331 StartZ=0 EndX=47.8912 EndY=20.2331 EndZ=0
    g351: LineSegment StartX=47.8912 StartY=20.2331 StartZ=0 EndX=47.8912 EndY=20.2962 EndZ=0
    g352: LineSegment StartX=47.8912 StartY=20.2962 StartZ=0 EndX=47.6864 EndY=20.2962 EndZ=0
    g353: LineSegment StartX=47.6864 StartY=20.2962 StartZ=0 EndX=47.6864 EndY=20.3681 EndZ=0
    g354: LineSegment StartX=47.6864 StartY=20.3681 StartZ=0 EndX=47.2898 EndY=20.3681 EndZ=0
    g355: LineSegment StartX=47.2898 StartY=20.3681 StartZ=0 EndX=47.2898 EndY=20.4313 EndZ=0
    g356: LineSegment StartX=47.2898 StartY=20.4313 StartZ=0 EndX=47.0094 EndY=20.4313 EndZ=0
    g357: LineSegment StartX=47.0094 StartY=20.4313 StartZ=0 EndX=47.0094 EndY=20.5033 EndZ=0
    g358: LineSegment StartX=47.0094 StartY=20.5033 StartZ=0 EndX=46.7265 EndY=20.5033 EndZ=0
    g359: LineSegment StartX=46.7265 StartY=20.5033 StartZ=0 EndX=46.7265 EndY=20.5623 EndZ=0
    g360: LineSegment StartX=46.7265 StartY=20.5623 StartZ=0 EndX=46.3195 EndY=20.5623 EndZ=0
    g361: LineSegment StartX=46.3195 StartY=20.5623 StartZ=0 EndX=46.2304 EndY=20.478 EndZ=0
    g362: LineSegment StartX=46.2304 StartY=20.478 StartZ=0 EndX=45.8403 EndY=20.478 EndZ=0
    g363: LineSegment StartX=45.8403 StartY=20.478 StartZ=0 EndX=45.7581 EndY=20.3987 EndZ=0
    g364: LineSegment StartX=45.7581 StartY=20.3987 StartZ=0 EndX=45.6847 EndY=20.3987 EndZ=0
    g365: LineSegment StartX=45.6847 StartY=20.3987 StartZ=0 EndX=45.6847 EndY=20.4757 EndZ=0
    g366: LineSegment StartX=45.6847 StartY=20.4757 StartZ=0 EndX=45.2353 EndY=20.4757 EndZ=0
    g367: LineSegment StartX=45.2353 StartY=20.4757 StartZ=0 EndX=45.1511 EndY=20.3964 EndZ=0
    g368: LineSegment StartX=45.1511 StartY=20.3964 StartZ=0 EndX=45.039 EndY=20.3905 EndZ=0
    g369: LineSegment StartX=45.1271 StartY=20.498 StartZ=0 EndX=45.039 EndY=20.3905 EndZ=0
    g370: LineSegment StartX=45.1271 StartY=20.498 StartZ=0 EndX=45.1672 EndY=20.498 EndZ=0
    g371: LineSegment StartX=45.1672 StartY=20.498 StartZ=0 EndX=45.2586 EndY=20.5605 EndZ=0
    g372: LineSegment StartX=45.2586 StartY=20.5605 StartZ=0 EndX=45.3242 EndY=20.5605 EndZ=0
    g373: LineSegment StartX=45.3242 StartY=20.5605 StartZ=0 EndX=45.4009 EndY=20.6461 EndZ=0
    g374: LineSegment StartX=45.4009 StartY=20.6461 StartZ=0 EndX=45.5221 EndY=20.6461 EndZ=0
    g375: LineSegment StartX=45.5221 StartY=20.6461 StartZ=0 EndX=45.6149 EndY=20.705 EndZ=0
    g376: LineSegment StartX=45.6149 StartY=20.705 StartZ=0 EndX=45.8042 EndY=20.705 EndZ=0
    g377: LineSegment StartX=45.8042 StartY=20.705 StartZ=0 EndX=45.9915 EndY=20.8898 EndZ=0
    g378: LineSegment StartX=45.9915 StartY=20.8898 StartZ=0 EndX=45.9915 EndY=20.959 EndZ=0
    g379: LineSegment StartX=45.9915 StartY=20.959 StartZ=0 EndX=46.0581 EndY=21.0202 EndZ=0
    g380: LineSegment StartX=46.0581 StartY=21.0202 StartZ=0 EndX=46.0527 EndY=21.0894 EndZ=0
    g381: LineSegment StartX=46.0527 StartY=21.0894 StartZ=0 EndX=46.2124 EndY=21.2464 EndZ=0
    g382: LineSegment StartX=46.2124 StartY=21.2464 StartZ=0 EndX=46.2763 EndY=21.2277 EndZ=0
    g383: LineSegment StartX=46.2763 StartY=21.2277 StartZ=0 EndX=46.5051 EndY=21.4486 EndZ=0
    g384: LineSegment StartX=46.5051 StartY=21.4486 StartZ=0 EndX=46.585 EndY=21.4539 EndZ=0
    g385: LineSegment StartX=46.585 StartY=21.4539 StartZ=0 EndX=46.6994 EndY=21.603 EndZ=0
    g386: LineSegment StartX=46.6994 StartY=21.603 StartZ=0 EndX=46.8245 EndY=21.5843 EndZ=0
    g387: LineSegment StartX=46.8245 StartY=21.5843 StartZ=0 EndX=46.9016 EndY=21.6855 EndZ=0
    g388: LineSegment StartX=46.9016 StartY=21.6855 StartZ=0 EndX=46.9655 EndY=21.6562 EndZ=0
    g389: LineSegment StartX=46.9655 StartY=21.6562 StartZ=0 EndX=47.205 EndY=21.8754 EndZ=0
    g390: LineSegment StartX=47.205 StartY=21.8754 StartZ=0 EndX=47.205 EndY=22.0711 EndZ=0
    g391: LineSegment StartX=47.205 StartY=22.0711 StartZ=0 EndX=47.2634 EndY=22.0711 EndZ=0
    g392: LineSegment StartX=47.2634 StartY=22.0711 StartZ=0 EndX=47.6208 EndY=22.4458 EndZ=0
    g393: LineSegment StartX=47.6208 StartY=22.4458 StartZ=0 EndX=47.6208 EndY=22.5177 EndZ=0
    g394: LineSegment StartX=47.6208 StartY=22.5177 StartZ=0 EndX=47.8212 EndY=22.7182 EndZ=0
    g395: LineSegment StartX=47.8212 StartY=22.7182 StartZ=0 EndX=47.8343 EndY=22.7944 EndZ=0
    g396: LineSegment StartX=47.8343 StartY=22.7944 StartZ=0 EndX=48.0478 EndY=22.997 EndZ=0
    g397: LineSegment StartX=48.0478 StartY=22.997 StartZ=0 EndX=48.0478 EndY=23.1365 EndZ=0
    g398: LineSegment StartX=48.0478 StartY=23.1365 StartZ=0 EndX=48.0998 EndY=23.2173 EndZ=0
    g399: LineSegment StartX=48.0998 StartY=23.2173 StartZ=0 EndX=48.0998 EndY=23.2802 EndZ=0
    ... +484 more geometry lines
  constraints (1492):
    c: Coincident(g3,g2)
    c: Vertical(g4)
    c: Vertical(g6)
    c: Coincident(g8,g7)
    c: Vertical(g8)
    c: Coincident(g8,g9)
    c: Coincident(g9,g10)
    c: Vertical(g10)
    c: Coincident(g10,g11)
    c: Coincident(g11,g12)
    c: Vertical(g12)
    c: Coincident(g13,g12)
    c: Horizontal(g13)
    c: Vertical(g14)
    c: Coincident(g16,g15)
    c: Vertical(g16)
    c: Horizontal(g17)
    c: Coincident(g18,g17)
    c: Vertical(g18)
    c: Horizontal(g19)
    c: Coincident(g20,g19)
    c: Vertical(g20)
    c: Horizontal(g21)
    c: Vertical(g22)
    c: Horizontal(g23)
    c: Coincident(g24,g23)
    c: Vertical(g24)
    c: Horizontal(g25)
    c: Coincident(g27,g26)
    c: Horizontal(g27)
    c: Vertical(g28)
    c: Coincident(g30,g29)
    c: Vertical(g30)
    c: Coincident(g31,g32)
    c: Vertical(g32)
    c: Coincident(g32,g33)
    c: Horizontal(g33)
    c: Coincident(g34,g33)
    c: Vertical(g34)
    c: Coincident(g35,g34)
    c: Horizontal(g35)
    c: Coincident(g36,g35)
    c: Vertical(g36)
    c: Coincident(g37,g36)
    c: Horizontal(g37)
    c: Vertical(g38)
    c: Horizontal(g39)
    c: Vertical(g40)
    c: Horizontal(g41)
    c: Coincident(g42,g41)
    c: Vertical(g42)
    c: Horizontal(g43)
    c: Coincident(g44,g43)
    c: Vertical(g44)
    c: Coincident(g45,g44)
    c: Horizontal(g45)
    c: Coincident(g46,g45)
    c: Vertical(g46)
    c: Coincident(g47,g46)
    c: Horizontal(g47)
    c: Coincident(g48,g47)
    c: Vertical(g48)
    c: Horizontal(g49)
    c: Vertical(g50)
    c: Coincident(g51,g50)
    c: Horizontal(g51)
    c: Vertical(g52)
    c: Coincident(g53,g52)
    c: Horizontal(g53)
    c: Coincident(g54,g53)
    c: Vertical(g54)
    c: Coincident(g55,g54)
    c: Horizontal(g55)
    c: Coincident(g56,g55)
    c: Vertical(g56)
    c: Coincident(g57,g56)
    c: Horizontal(g57)
    c: Coincident(g58,g57)
    c: Vertical(g58)
    c: Coincident(g60,g59)
    c: Vertical(g60)
    c: Coincident(g61,g60)
    c: Horizontal(g61)
    c: Vertical(g62)
    c: Horizontal(g63)
    c: Coincident(g64,g63)
    c: Vertical(g64)
    c: Horizontal(g65)
    c: Vertical(g66)
    c: Coincident(g68,g67)
    c: Vertical(g68)
    c: Horizontal(g69)
    c: Coincident(g70,g69)
    c: Vertical(g70)
    c: Horizontal(g71)
    c: Coincident(g72,g71)
    c: Vertical(g72)
    c: Horizontal(g73)
    c: Coincident(g74,g73)
    c: Vertical(g74)
    c: Horizontal(g75)
    c: Coincident(g76,g75)
    c: Vertical(g76)
    c: Horizontal(g77)
    c: Vertical(g78)
    c: Coincident(g79,g78)
    c: Coincident(g80,g79)
    c: Vertical(g80)
    c: Coincident(g81,g80)
    c: Coincident(g82,g81)
    c: Horizontal(g83)
    c: Coincident(g85,g84)
    c: Horizontal(g85)
    c: Coincident(g86,g85)
    c: Coincident(g89,g88)
    c: Horizontal(g89)
    c: Coincident(g90,g89)
    c: Coincident(g91,g90)
    c: Horizontal(g91)
    c: Coincident(g92,g91)
    c: Horizontal(g93)
    c: Coincident(g94,g93)
    c: Horizontal(g95)
    c: Coincident(g96,g95)
    c: Coincident(g97,g98)
    c: Coincident(g98,g99)
    c: Vertical(g99)
    c: Coincident(g99,g100)
    c: Coincident(g100,g101)
    c: Coincident(g101,g102)
    c: Coincident(g102,g103)
    c: Coincident(g103,g104)
    c: Coincident(g104,g105)
    c: Vertical(g105)
    c: Coincident(g105,g106)
    c: Coincident(g106,g107)
    c: Coincident(g107,g108)
    c: Horizontal(g108)
    c: Coincident(g108,g109)
    c: Coincident(g109,g110)
    c: Vertical(g110)
    c: Coincident(g110,g111)
    c: Coincident(g111,g112)
    c: Coincident(g112,g113)
    c: Coincident(g113,g114)
    c: Coincident(g114,g115)
    c: Coincident(g115,g116)
    c: Vertical(g116)
    c: Coincident(g116,g117)
    c: Coincident(g117,g118)
    c: Coincident(g118,g119)
    c: Coincident(g119,g120)
    c: Coincident(g120,g121)
    c: Horizontal(g121)
    c: Coincident(g121,g122)
    c: Coincident(g122,g123)
    c: Coincident(g123,g124)
    c: Coincident(g124,g125)
    c: Vertical(g125)
    c: Coincident(g125,g126)
    c: Coincident(g126,g127)
    c: Horizontal(g127)
    c: Coincident(g127,g128)
    c: Vertical(g128)
    c: Coincident(g128,g129)
    c: Coincident(g129,g130)
    c: Vertical(g130)
    c: Coincident(g130,g131)
    c: Horizontal(g131)
    c: Coincident(g131,g132)
    c: Vertical(g132)
    c: Coincident(g132,g133)
    c: Coincident(g133,g134)
    c: Coincident(g134,g135)
    c: Coincident(g135,g136)
    c: Coincident(g136,g137)
    c: Coincident(g137,g138)
    c: Vertical(g138)
    c: Coincident(g138,g139)
    c: Coincident(g139,g140)
    c: Vertical(g140)
    c: Coincident(g140,g141)
    c: Horizontal(g141)
    c: Coincident(g141,g142)
    c: Coincident(g142,g143)
    c: Coincident(g143,g144)
    c: Coincident(g144,g145)
    c: Coincident(g145,g146)
    c: Vertical(g146)
    c: Coincident(g146,g147)
    c: Coincident(g147,g148)
    c: Vertical(g148)
    c: Coincident(g148,g149)
    c: Horizontal(g149)
    c: Coincident(g149,g150)
    c: Vertical(g150)
    c: Coincident(g150,g151)
    c: Horizontal(g151)
    c: Coincident(g151,g152)
    c: Vertical(g152)
    c: Coincident(g152,g153)
    c: Horizontal(g153)
    c: Coincident(g153,g154)
    c: Vertical(g154)
    c: Coincident(g154,g155)
    c: Horizontal(g155)
    c: Coincident(g155,g156)
    c: Vertical(g156)
    c: Coincident(g156,g157)
    c: Horizontal(g157)
    c: Coincident(g157,g158)
    c: Vertical(g158)
    c: Coincident(g158,g159)
    c: Coincident(g159,g160)
    c: Coincident(g160,g161)
    c: Horizontal(g161)
    c: Coincident(g161,g162)
    c: Vertical(g162)
    c: Coincident(g162,g163)
    c: Horizontal(g163)
    c: Coincident(g163,g164)
    c: Coincident(g164,g165)
    c: Horizontal(g165)
    c: Coincident(g165,g166)
    c: Vertical(g166)
    c: Coincident(g166,g167)
    c: Horizontal(g167)
    c: Coincident(g167,g168)
    c: Coincident(g168,g169)
    c: Coincident(g169,g170)
    c: Vertical(g170)
    c: Coincident(g170,g171)
    c: Coincident(g171,g172)
    c: Vertical(g172)
    c: Coincident(g172,g173)
    c: Horizontal(g173)
    c: Coincident(g173,g174)
    c: Vertical(g174)
    c: Coincident(g174,g175)
    c: Horizontal(g175)
    c: Coincident(g175,g176)
    c: Vertical(g176)
    c: Coincident(g176,g177)
    c: Coincident(g177,g178)
    c: Vertical(g178)
    c: Coincident(g178,g179)
    c: Horizontal(g179)
    c: Coincident(g179,g180)
    c: Vertical(g180)
    c: Coincident(g180,g181)
    c: Horizontal(g181)
    c: Coincident(g181,g182)
    c: Vertical(g182)
    c: Coincident(g182,g183)
    c: Horizontal(g183)
    c: Coincident(g183,g184)
    c: Vertical(g184)
    c: Coincident(g184,g185)
    c: Horizontal(g185)
    c: Coincident(g185,g186)
    c: Coincident(g186,g187)
    c: Coincident(g187,g188)
    c: Coincident(g188,g189)
    c: Vertical(g189)
    c: Coincident(g189,g190)
    c: Coincident(g190,g191)
    c: Coincident(g191,g192)
    c: Coincident(g192,g193)
    c: Coincident(g193,g194)
    c: Coincident(g194,g195)
    c: Vertical(g195)
    c: Coincident(g195,g196)
    c: Coincident(g196,g197)
    c: Vertical(g197)
    c: Coincident(g197,g198)
    c: Coincident(g198,g199)
    c: Vertical(g199)
    c: Coincident(g199,g200)
    c: Coincident(g200,g201)
    c: Vertical(g201)
    c: Coincident(g201,g202)
    c: Coincident(g202,g203)
    c: Vertical(g203)
    c: Coincident(g203,g204)
    c: Coincident(g204,g205)
    c: Vertical(g205)
    c: Coincident(g205,g206)
    c: Coincident(g206,g207)
    c: Coincident(g207,g208)
    c: Coincident(g208,g209)
    c: Vertical(g209)
    c: Coincident(g209,g210)
    c: Coincident(g210,g211)
    c: Coincident(g211,g212)
    c: Coincident(g212,g213)
    c: Coincident(g213,g214)
    c: Coincident(g214,g215)
    c: Vertical(g215)
    c: Coincident(g215,g216)
    c: Coincident(g216,g217)
    c: Horizontal(g217)
    c: Coincident(g217,g218)
    c: Vertical(g218)
    c: Coincident(g218,g219)
    c: Horizontal(g219)
    c: Coincident(g219,g220)
    c: Coincident(g220,g221)
    c: Horizontal(g221)
    c: Coincident(g221,g222)
    c: Coincident(g222,g223)
    c: Horizontal(g223)
    c: Coincident(g223,g224)
    c: Coincident(g224,g225)
    c: Horizontal(g225)
    c: Coincident(g225,g226)
    c: Vertical(g226)
    c: Coincident(g226,g227)
    c: Horizontal(g227)
    c: Coincident(g227,g228)
    c: Vertical(g228)
    c: Coincident(g228,g229)
    c: Horizontal(g229)
    c: Coincident(g229,g230)
    c: Coincident(g230,g231)
    c: Coincident(g231,g232)
    c: Coincident(g232,g233)
    c: Horizontal(g233)
    c: Coincident(g233,g234)
    c: Coincident(g234,g235)
    c: Horizontal(g235)
    c: Coincident(g235,g236)
    c: Coincident(g236,g237)
    c: Horizontal(g237)
    c: Coincident(g237,g238)
    c: Coincident(g238,g239)
    c: Horizontal(g239)
    c: Coincident(g239,g240)
    c: Coincident(g240,g241)
    c: Vertical(g241)
    c: Coincident(g241,g242)
    c: Horizontal(g242)
    c: Coincident(g242,g243)
    c: Vertical(g243)
    c: Coincident(g243,g244)
    c: Coincident(g244,g245)
    c: Vertical(g245)
    c: Coincident(g245,g246)
    c: Horizontal(g246)
    c: Coincident(g246,g247)
    c: Coincident(g247,g248)
    c: Horizontal(g248)
    c: Coincident(g248,g249)
    c: Vertical(g249)
    c: Coincident(g249,g250)
    c: Coincident(g250,g251)
    c: Coincident(g251,g252)
    c: Horizontal(g252)
    c: Coincident(g252,g253)
    c: Coincident(g253,g254)
    c: Horizontal(g254)
    c: Coincident(g254,g255)
    c: Vertical(g255)
    c: Coincident(g255,g256)
    c: Coincident(g256,g257)
    c: Coincident(g257,g258)
    c: Coincident(g258,g259)
    c: Coincident(g259,g260)
    c: Coincident(g260,g261)
    c: Vertical(g257)
    c: Horizontal(g258)
    c: Horizontal(g256)
    c: Vertical(g259)
    c: Horizontal(g260)
    c: Vertical(g261)
    c: Coincident(g261,g262)
    c: Horizontal(g262)
    c: Coincident(g262,g263)
    c: Vertical(g263)
    c: Coincident(g263,g264)
    c: Coincident(g264,g265)
    c: Coincident(g265,g266)
    c: Coincident(g266,g267)
    c: Coincident(g267,g268)
    c: Coincident(g268,g269)
    c: Vertical(g269)
    c: Coincident(g269,g270)
    c: Horizontal(g270)
    c: Coincident(g270,g271)
    c: Vertical(g271)
    c: Coincident(g271,g272)
    c: Coincident(g272,g273)
    c: Vertical(g273)
    c: Coincident(g273,g274)
    c: Horizontal(g274)
    c: Coincident(g274,g275)
    c: Vertical(g275)
    c: Coincident(g275,g276)
    c: Horizontal(g276)
    c: Coincident(g276,g277)
    c: Coincident(g277,g278)
    c: Horizontal(g278)
    c: Coincident(g278,g279)
    c: Coincident(g279,g280)
    c: Coincident(g280,g281)
    c: Vertical(g281)
    c: Coincident(g281,g282)
    c: Coincident(g282,g283)
    c: Coincident(g283,g284)
    c: Horizontal(g284)
    c: Coincident(g284,g285)
    c: Coincident(g285,g286)
    c: Coincident(g286,g287)
    c: Coincident(g287,g288)
    c: Coincident(g288,g289)
    c: Coincident(g289,g290)
    c: Coincident(g290,g291)
    c: Vertical(g291)
    c: Coincident(g291,g292)
    c: Horizontal(g292)
    c: Coincident(g292,g293)
    c: Coincident(g293,g294)
    c: Horizontal(g294)
    c: Coincident(g294,g295)
    c: Vertical(g295)
    c: Coincident(g295,g296)
    c: Coincident(g296,g297)
    c: Vertical(g297)
    c: Coincident(g297,g298)
    c: Horizontal(g298)
    c: Coincident(g298,g299)
    c: Vertical(g299)
    c: Coincident(g299,g300)
    c: Horizontal(g300)
    c: Coincident(g300,g301)
    c: Coincident(g301,g302)
    c: Coincident(g302,g303)
    c: Coincident(g303,g304)
    c: Coincident(g304,g305)
    c: Coincident(g305,g306)
    c: Coincident(g306,g307)
    c: Coincident(g307,g308)
    c: Horizontal(g308)
    c: Coincident(g308,g309)
    c: Coincident(g309,g310)
    c: Horizontal(g310)
    c: Coincident(g310,g311)
    c: Coincident(g311,g312)
    c: Coincident(g312,g313)
    c: Coincident(g313,g314)
    c: Coincident(g314,g315)
    c: Coincident(g315,g316)
    c: Coincident(g316,g317)
    c: Coincident(g317,g318)
    c: Coincident(g318,g319)
    c: Coincident(g319,g320)
    c: Coincident(g320,g321)
    c: Coincident(g321,g322)
    c: Coincident(g322,g323)
    c: Coincident(g323,g324)
    c: Horizontal(g324)
    c: Coincident(g324,g325)
    c: Coincident(g325,g326)
    c: Coincident(g326,g327)
    c: Vertical(g327)
    c: Coincident(g327,g328)
    c: Coincident(g328,g329)
    c: Coincident(g329,g330)
    c: Coincident(g330,g331)
    c: Vertical(g331)
    c: Coincident(g331,g332)
    c: Coincident(g332,g333)
    c: Coincident(g333,g334)
    c: Coincident(g334,g335)
    c: Coincident(g335,g336)
    c: Coincident(g336,g337)
    c: Vertical(g337)
    c: Coincident(g337,g338)
    c: Coincident(g338,g339)
    c: Coincident(g339,g340)
    c: Coincident(g340,g341)
    c: Coincident(g341,g342)
    c: Coincident(g342,g343)
    c: Coincident(g343,g344)
    c: Coincident(g344,g345)
    c: Coincident(g345,g346)
    c: Coincident(g346,g347)
    c: Coincident(g347,g348)
    c: Coincident(g348,g349)
    c: Coincident(g349,g350)
    c: Coincident(g350,g351)
    c: Coincident(g351,g352)
    c: Coincident(g352,g353)
    c: Coincident(g353,g354)
    c: Coincident(g354,g355)
    c: Coincident(g355,g356)
    c: Coincident(g356,g357)
    c: Vertical(g357)
    c: Coincident(g357,g358)
    c: Horizontal(g358)
    c: Coincident(g358,g359)
    c: Coincident(g359,g360)
    c: Coincident(g360,g361)
    c: Coincident(g361,g362)
    c: Horizontal(g362)
    c: Coincident(g362,g363)
    c: Coincident(g363,g364)
    c: Coincident(g364,g365)
    c: Coincident(g365,g366)
    c: Coincident(g366,g367)
    c: Horizontal(g290)
    c: Vertical(g287)
    c: Vertical(g285)
    c: Vertical(g283)
    c: Vertical(g279)
    c: Vertical(g277)
    c: Horizontal(g286)
    c: Horizontal(g288)
    c: Vertical(g289)
    c: Horizontal(g280)
    c: Horizontal(g282)
    c: Vertical(g329)
    c: Horizontal(g330)
    c: Horizontal(g340)
    c: Horizontal(g342)
    c: Horizontal(g344)
    c: Horizontal(g346)
    c: Horizontal(g348)
    c: Horizontal(g350)
    c: Vertical(g339)
    c: Vertical(g341)
    c: Vertical(g343)
    c: Vertical(g345)
    c: Vertical(g347)
    c: Vertical(g349)
    c: Vertical(g351)
    c: Vertical(g353)
    c: Vertical(g355)
    c: Horizontal(g352)
    c: Horizontal(g354)
    c: Horizontal(g356)
    c: Vertical(g359)
    c: Horizontal(g360)
    c: Horizontal(g364)
    c: Vertical(g365)
    c: Horizontal(g366)
    c: Coincident(g368,g367)
    c: Coincident(g369,g368)
    c: Coincident(g369,g370)
    c: Coincident(g370,g371)
    c: Coincident(g371,g372)
    c: Horizontal(g372)
    c: Coincident(g372,g373)
    c: Coincident(g373,g374)
    c: Coincident(g374,g375)
    c: Coincident(g375,g376)
    c: Coincident(g376,g377)
    c: Coincident(g377,g378)
    c: Vertical(g378)
    c: Coincident(g378,g379)
    c: Coincident(g379,g380)
    c: Coincident(g380,g381)
    c: Coincident(g381,g382)
    c: Coincident(g382,g383)
    c: Coincident(g383,g384)
    c: Coincident(g384,g385)
    c: Coincident(g385,g386)
    c: Coincident(g386,g387)
    c: Coincident(g387,g388)
    c: Coincident(g388,g389)
    c: Coincident(g389,g390)
    c: Coincident(g390,g391)
    c: Horizontal(g391)
    c: Coincident(g391,g392)
    c: Coincident(g392,g393)
    c: Coincident(g393,g394)
    c: Coincident(g394,g395)
    c: Coincident(g395,g396)
    c: Coincident(g396,g397)
    c: Coincident(g397,g398)
    c: Coincident(g398,g399)
    c: Coincident(g399,g400)
    c: Coincident(g400,g401)
    c: Coincident(g401,g402)
    c: Coincident(g402,g403)
    c: Coincident(g403,g404)
    c: Coincident(g404,g405)
    c: Coincident(g405,g406)
    c: Coincident(g406,g407)
    c: Coincident(g407,g408)
    c: Coincident(g408,g409)
    c: Vertical(g409)
    c: Coincident(g409,g410)
    c: Coincident(g410,g411)
    c: Vertical(g411)
    c: Coincident(g411,g412)
    c: Horizontal(g412)
    c: Coincident(g412,g413)
    c: Coincident(g413,g414)
    c: Horizontal(g414)
    c: Coincident(g414,g415)
    c: Coincident(g415,g416)
    c: Coincident(g416,g417)
    c: Coincident(g417,g418)
    c: Coincident(g418,g419)
    c: Coincident(g419,g420)
    c: Coincident(g420,g421)
    c: Coincident(g421,g422)
    c: Coincident(g422,g423)
    c: Coincident(g423,g424)
    c: Coincident(g424,g425)
    c: Coincident(g425,g426)
    c: Horizontal(g426)
    c: Coincident(g426,g427)
    c: Coincident(g427,g428)
    c: Horizontal(g428)
    c: Coincident(g428,g429)
    c: Coincident(g429,g430)
    c: Coincident(g430,g431)
    c: Coincident(g431,g432)
    c: Horizontal(g432)
    c: Coincident(g432,g433)
    c: Coincident(g433,g434)
    c: Horizontal(g434)
    c: Coincident(g434,g435)
    c: Coincident(g435,g436)
    c: Coincident(g436,g437)
    c: Coincident(g437,g438)
    c: Coincident(g439,g440)
    c: Coincident(g440,g441)
    c: Coincident(g441,g442)
    c: Coincident(g442,g443)
    c: Coincident(g443,g444)
    c: Coincident(g444,g445)
    c: Coincident(g445,g446)
    c: Coincident(g446,g447)
    c: Coincident(g447,g448)
    c: Coincident(g448,g449)
    c: Coincident(g449,g450)
    c: Coincident(g450,g451)
    c: Coincident(g451,g452)
    c: Coincident(g452,g453)
    c: Coincident(g453,g454)
    c: Coincident(g454,g455)
    c: Coincident(g455,g456)
    c: Coincident(g456,g457)
    c: Coincident(g457,g458)
    c: Coincident(g458,g459)
    c: Coincident(g459,g460)
    c: Coincident(g460,g461)
    c: Coincident(g461,g462)
    c: Coincident(g462,g463)
    c: Coincident(g463,g464)
    c: Coincident(g464,g465)
    c: Coincident(g465,g466)
    c: Coincident(g466,g467)
    c: Coincident(g467,g468)
    c: Coincident(g468,g469)
    c: Coincident(g469,g470)
    c: Coincident(g470,g471)
    c: Coincident(g471,g472)
    c: Horizontal(g472)
    c: Coincident(g472,g473)
    c: Coincident(g473,g474)
    c: Coincident(g474,g475)
    c: Coincident(g475,g476)
    c: Coincident(g476,g477)
    c: Coincident(g477,g478)
    c: Coincident(g478,g479)
    c: Coincident(g479,g480)
    c: Coincident(g480,g481)
    c: Coincident(g481,g482)
    c: Coincident(g482,g483)
    c: Coincident(g483,g484)
    c: Coincident(g484,g485)
    c: Coincident(g485,g486)
    c: Coincident(g486,g487)
    c: Coincident(g487,g488)
    c: Vertical(g488)
    c: Coincident(g488,g489)
    c: Coincident(g489,g490)
    c: Vertical(g490)
    c: Coincident(g490,g491)
    c: Coincident(g491,g492)
    c: Coincident(g492,g493)
    c: Coincident(g493,g494)
    c: Coincident(g494,g495)
    c: Coincident(g495,g496)
    c: Coincident(g496,g497)
    c: Coincident(g497,g498)
    c: Coincident(g498,g499)
    c: Coincident(g499,g500)
    c: Coincident(g500,g501)
    c: Coincident(g501,g502)
    c: Coincident(g502,g503)
    c: Coincident(g503,g504)
    c: Horizontal(g370)
    c: Horizontal(g374)
    c: Horizontal(g376)
    c: Vertical(g390)
    c: Vertical(g397)
    c: Vertical(g399)
    c: Vertical(g401)
    c: Vertical(g403)
    c: Vertical(g407)
    c: Horizontal(g410)
    c: Vertical(g413)
    c: Vertical(g415)
    c: Horizontal(g416)
    c: Vertical(g417)
    c: Horizontal(g418)
    c: Vertical(g419)
    c: Vertical(g421)
    c: Vertical(g423)
    c: Vertical(g425)
    c: Vertical(g427)
    c: Vertical(g429)
    c: Horizontal(g420)
    c: Horizontal(g422)
    c: Horizontal(g424)
    c: Vertical(g431)
    c: Vertical(g433)
    c: Vertical(g435)
    c: Horizontal(g436)
    c: Horizontal(g438)
    c: Vertical(g437)
    c: Coincident(g439,g505)
    c: Horizontal(g505)
    c: Coincident(g505,g506)
    c: Coincident(g506,g438)
    c: Vertical(g506)
    c: Horizontal(g464)
    c: Horizontal(g462)
    c: Horizontal(g460)
    c: Horizontal(g458)
    c: Horizontal(g456)
    c: Horizontal(g454)
    c: Horizontal(g452)
    c: Horizontal(g450)
    c: Horizontal(g448)
    c: Horizontal(g446)
    c: Horizontal(g444)
    c: Horizontal(g442)
    c: Horizontal(g440)
    c: Horizontal(g468)
    c: Horizontal(g470)
    c: Horizontal(g474)
    c: Horizontal(g476)
    c: Horizontal(g478)
    c: Vertical(g465)
    c: Horizontal(g466)
    c: Vertical(g475)
    c: Vertical(g477)
    c: Horizontal(g491)
    c: Horizontal(g496)
    c: Horizontal(g494)
    c: Horizontal(g498)
    c: Vertical(g499)
    c: Vertical(g497)
    c: Vertical(g495)
    c: Vertical(g493)
    c: Horizontal(g500)
    c: Horizontal(g502)
    c: Horizontal(g504)
    c: Vertical(g501)
    c: Vertical(g503)
    c: Coincident(g504,g507)
    c: Vertical(g507)
    c: Coincident(g507,g508)
    c: Coincident(g508,g509)
    c: Coincident(g509,g510)
    c: Coincident(g510,g511)
    c: Vertical(g511)
    c: Coincident(g511,g512)
    c: Horizontal(g512)
    c: Coincident(g512,g513)
    c: Vertical(g513)
    c: Coincident(g513,g514)
    c: Coincident(g514,g515)
    c: Vertical(g515)
    c: Coincident(g515,g516)
    c: Horizontal(g516)
    c: Coincident(g516,g517)
    c: Coincident(g517,g518)
    c: Horizontal(g518)
    c: Coincident(g518,g519)
    c: Coincident(g519,g520)
    c: Coincident(g521,g522)
    c: Coincident(g522,g523)
    c: Coincident(g523,g524)
    c: Coincident(g524,g525)
    c: Coincident(g525,g526)
    c: Coincident(g526,g527)
    c: Coincident(g527,g528)
    c: Coincident(g528,g529)
    c: Coincident(g529,g530)
    c: Coincident(g531,g532)
    c: Coincident(g532,g533)
    c: Coincident(g533,g534)
    c: Coincident(g534,g535)
    c: Coincident(g535,g536)
    c: Coincident(g536,g537)
    c: Coincident(g537,g538)
    c: Coincident(g538,g539)
    c: Coincident(g539,g540)
    c: Coincident(g540,g541)
    c: Coincident(g541,g542)
    c: Coincident(g542,g543)
    c: Coincident(g543,g544)
    c: Coincident(g544,g545)
    c: Coincident(g545,g546)
    c: Coincident(g546,g547)
    c: Coincident(g547,g548)
    c: Coincident(g548,g549)
    c: Coincident(g549,g550)
    c: Horizontal(g550)
    c: Coincident(g550,g551)
    c: Coincident(g551,g552)
    c: Coincident(g552,g553)
    c: Coincident(g553,g554)
    c: Horizontal(g554)
    c: Coincident(g554,g555)
    c: Coincident(g555,g556)
    c: Coincident(g556,g557)
    c: Coincident(g557,g558)
    c: Horizontal(g558)
    c: Coincident(g558,g559)
    c: Coincident(g559,g560)
    c: Coincident(g560,g561)
    c: Coincident(g562,g563)
    c: Horizontal(g563)
    c: Coincident(g563,g564)
    c: Coincident(g564,g565)
    c: Coincident(g565,g566)
    c: Coincident(g566,g567)
    c: Horizontal(g567)
    c: Coincident(g567,g568)
    c: Coincident(g568,g569)
    c: Coincident(g569,g570)
    c: Coincident(g570,g571)
    c: Coincident(g571,g572)
    c: Coincident(g572,g573)
    c: Coincident(g573,g574)
    c: Coincident(g574,g575)
    c: Coincident(g575,g576)
    c: Coincident(g576,g577)
    c: Coincident(g577,g578)
    c: Coincident(g578,g579)
    c: Coincident(g579,g580)
    c: Vertical(g580)
    c: Coincident(g580,g581)
    c: Coincident(g581,g582)
    c: Coincident(g582,g583)
    c: Coincident(g583,g584)
    c: Coincident(g584,g585)
    c: Horizontal(g585)
    c: Coincident(g585,g586)
    c: Coincident(g586,g587)
    c: Coincident(g587,g588)
    c: Vertical(g588)
    c: Coincident(g588,g589)
    c: Coincident(g589,g590)
    c: Coincident(g590,g591)
    c: Coincident(g592,g593)
    c: Horizontal(g593)
    c: Coincident(g593,g594)
    c: Coincident(g594,g595)
    c: Coincident(g595,g596)
    c: Vertical(g596)
    c: Coincident(g596,g597)
    c: Horizontal(g597)
    c: Coincident(g597,g598)
    c: Vertical(g598)
    c: Coincident(g598,g599)
    c: Coincident(g599,g600)
    c: Coincident(g600,g601)
    c: Horizontal(g601)
    c: Coincident(g601,g602)
    c: Coincident(g602,g603)
    c: Coincident(g603,g604)
    c: Coincident(g604,g605)
    c: Coincident(g605,g606)
    c: Coincident(g606,g607)
    c: Coincident(g607,g608)
    c: Coincident(g608,g609)
    c: Horizontal(g609)
    c: Coincident(g609,g610)
    c: Coincident(g610,g611)
    c: Coincident(g611,g612)
    c: Coincident(g612,g613)
    c: Vertical(g613)
    c: Coincident(g613,g614)
    c: Coincident(g614,g615)
    c: Vertical(g615)
    c: Coincident(g615,g616)
    c: Coincident(g616,g617)
    c: Vertical(g617)
    c: Coincident(g618,g619)
    c: Vertical(g619)
    c: Coincident(g619,g620)
    c: Coincident(g620,g621)
    c: Coincident(g621,g622)
    c: Coincident(g622,g623)
    c: Coincident(g623,g624)
    c: Coincident(g624,g625)
    c: Coincident(g625,g626)
    c: Coincident(g626,g627)
    c: Vertical(g627)
    c: Coincident(g627,g628)
    c: Coincident(g628,g629)
    c: Coincident(g629,g630)
    c: Coincident(g630,g631)
    c: Coincident(g631,g632)
    c: Coincident(g632,g633)
    c: Vertical(g633)
    c: Coincident(g633,g634)
    c: Coincident(g634,g635)
    c: Vertical(g635)
    c: Coincident(g635,g636)
    c: Coincident(g636,g637)
    c: Coincident(g637,g638)
    c: Coincident(g638,g639)
    c: Coincident(g639,g640)
    c: Horizontal(g640)
    c: Coincident(g640,g641)
    c: Coincident(g641,g642)
    c: Vertical(g642)
    c: Coincident(g642,g643)
    c: Coincident(g643,g644)
    c: Vertical(g644)
    c: Coincident(g644,g645)
    c: Coincident(g645,g646)
    c: Coincident(g646,g647)
    c: Coincident(g647,g648)
    c: Coincident(g648,g649)
    c: Coincident(g649,g650)
    c: Coincident(g650,g651)
    c: Coincident(g651,g652)
    c: Vertical(g652)
    c: Coincident(g652,g653)
    c: Coincident(g653,g654)
    c: Coincident(g654,g655)
    c: Coincident(g655,g656)
    c: Coincident(g656,g657)
    c: Coincident(g657,g658)
    c: Vertical(g658)
    c: Coincident(g658,g659)
    c: Coincident(g659,g660)
    c: Vertical(g660)
    c: Coincident(g660,g661)
    c: Coincident(g661,g662)
    c: Coincident(g662,g663)
    c: Coincident(g663,g664)
    c: Coincident(g664,g665)
    c: Coincident(g665,g666)
    c: Coincident(g666,g667)
    c: Coincident(g667,g668)
    c: Coincident(g668,g669)
    c: Coincident(g669,g670)
    c: Coincident(g670,g671)
    c: Coincident(g671,g672)
    c: Coincident(g672,g673)
    c: Horizontal(g673)
    c: Coincident(g673,g674)
    c: Coincident(g674,g675)
    c: Coincident(g675,g676)
    c: Coincident(g676,g677)
    c: Coincident(g677,g678)
    c: Vertical(g678)
    c: Coincident(g678,g679)
    c: Coincident(g680,g681)
    c: Vertical(g681)
    c: Coincident(g681,g682)
    c: Horizontal(g682)
    c: Coincident(g682,g683)
    c: Coincident(g683,g684)
    c: Coincident(g684,g685)
    c: Coincident(g685,g686)
    c: Coincident(g686,g687)
    c: Vertical(g687)
    c: Coincident(g687,g688)
    c: Coincident(g688,g689)
    c: Coincident(g689,g690)
    c: Coincident(g690,g691)
    c: Coincident(g691,g692)
    c: Coincident(g692,g693)
    c: Coincident(g693,g694)
    c: Horizontal(g694)
    c: Coincident(g694,g695)
    c: Horizontal(g508)
    c: Vertical(g509)
    c: Horizontal(g510)
    c: Vertical(g519)
    c: Vertical(g517)
    c: Horizontal(g520)
    c: Coincident(g520,g696)
    c: Coincident(g696,g697)
    c: Horizontal(g697)
    c: Coincident(g697,g698)
    c: Coincident(g698,g521)
    c: Vertical(g698)
    c: Vertical(g522)
    c: Vertical(g524)
    c: Vertical(g526)
    c: Horizontal(g523)
    c: Horizontal(g525)
    c: Horizontal(g527)
    c: Horizontal(g529)
    c: Horizontal(g532)
    c: Horizontal(g521)
    c: Vertical(g528)
    c: Vertical(g530)
    c: Coincident(g530,g699)
    c: Coincident(g699,g700)
    c: Coincident(g700,g701)
    c: Coincident(g701,g531)
    c: Vertical(g700)
    c: Vertical(g531)
    c: Vertical(g533)
    c: Vertical(g535)
    c: Vertical(g537)
    c: Vertical(g539)
    c: Vertical(g541)
    c: Horizontal(g534)
    c: Horizontal(g536)
    c: Horizontal(g538)
    c: Horizontal(g540)
    c: Horizontal(g542)
    c: Horizontal(g544)
    c: Horizontal(g546)
    c: Horizontal(g699)
    c: Horizontal(g701)
    c: Vertical(g543)
    c: Vertical(g545)
    c: Vertical(g547)
    c: Vertical(g549)
    c: Horizontal(g548)
    c: Vertical(g555)
    c: Vertical(g553)
    c: Vertical(g551)
    c: Horizontal(g552)
    c: Horizontal(g556)
    c: Horizontal(g560)
    c: Vertical(g557)
    c: Vertical(g559)
    c: Vertical(g561)
    c: Coincident(g702,g562)
    c: Coincident(g702,g561)
    c: Horizontal(g565)
    c: Horizontal(g569)
    c: Horizontal(g571)
    c: Horizontal(g573)
    c: Horizontal(g575)
    c: Horizontal(g702)
    c: Vertical(g566)
    c: Vertical(g568)
    c: Vertical(g570)
    c: Vertical(g572)
    c: Vertical(g574)
    c: Vertical(g576)
    c: Vertical(g578)
    c: Vertical(g582)
    c: Vertical(g584)
    c: Horizontal(g577)
    c: Horizontal(g579)
    c: Horizontal(g581)
    c: Horizontal(g583)
    c: Horizontal(g587)
    c: Horizontal(g589)
    c: Horizontal(g591)
    c: Coincident(g591,g592)
    c: Vertical(g590)
    c: Vertical(g592)
    c: Vertical(g594)
    c: Vertical(g602)
    c: Vertical(g604)
    c: Horizontal(g595)
    c: Horizontal(g599)
    c: Horizontal(g605)
    c: Horizontal(g607)
    c: Vertical(g608)
    c: Vertical(g611)
    c: Horizontal(g612)
    c: Horizontal(g614)
    c: Horizontal(g620)
    c: Horizontal(g622)
    c: Vertical(g621)
    c: Vertical(g623)
    c: Coincident(g618,g703)
    c: Vertical(g703)
    c: Coincident(g703,g704)
    c: Horizontal(g704)
    c: Coincident(g704,g617)
    c: Horizontal(g624)
    c: Vertical(g625)
    c: Horizontal(g643)
    c: Horizontal(g645)
    c: Horizontal(g647)
    c: Horizontal(g649)
    c: Horizontal(g651)
    c: Horizontal(g653)
    c: Horizontal(g655)
    c: Horizontal(g657)
    c: Horizontal(g659)
    c: Vertical(g656)
    c: Vertical(g654)
    c: Vertical(g650)
    c: Vertical(g648)
    c: Vertical(g646)
    c: Vertical(g637)
    c: Vertical(g639)
    c: Horizontal(g661)
    c: Horizontal(g663)
    c: Horizontal(g665)
    c: Horizontal(g667)
    c: Horizontal(g669)
    c: Horizontal(g671)
    c: Horizontal(g675)
    c: Vertical(g662)
    c: Vertical(g664)
    c: Vertical(g666)
    c: Vertical(g668)
    c: Vertical(g670)
    c: Vertical(g672)
    c: Vertical(g674)
    c: Vertical(g676)
    c: Horizontal(g677)
    c: Horizontal(g679)
    c: Coincident(g679,g705)
    c: Vertical(g705)
    c: Coincident(g705,g706)
    c: Horizontal(g706)
    c: Coincident(g706,g707)
    c: Coincident(g680,g707)
    c: Horizontal(g680)
    c: Vertical(g707)
    c: Vertical(g691)
    c: Vertical(g693)
    c: Vertical(g689)
    c: Vertical(g685)
    c: Vertical(g683)
    c: Horizontal(g686)
    c: Horizontal(g688)
    c: Horizontal(g690)
    c: Horizontal(g692)
    c: Horizontal(g684)
    c: Vertical(g695)
    c: Coincident(g695,g708)
    c: Coincident(g708,g709)
    c: Coincident(g709,g710)
    c: Coincident(g710,g711)
    c: Coincident(g711,g712)
    c: Coincident(g712,g713)
    c: Horizontal(g713)
    c: Coincident(g713,g714)
    c: Coincident(g714,g715)
    c: Coincident(g715,g716)
    c: Coincident(g716,g717)
    c: Coincident(g718,g719)
    c: Horizontal(g720)
    c: Coincident(g721,g722)
    c: Coincident(g722,g723)
    c: Coincident(g723,g724)
    c: Horizontal(g724)
    c: Coincident(g724,g725)
    c: Horizontal(g726)
    c: Coincident(g726,g727)
    c: Coincident(g727,g728)
    c: Horizontal(g728)
    c: Coincident(g728,g729)
    c: Coincident(g729,g730)
    c: Coincident(g730,g731)
    c: Coincident(g731,g732)
    c: Coincident(g732,g733)
    c: Coincident(g733,g734)
    c: Coincident(g734,g735)
    c: Coincident(g735,g736)
    c: Coincident(g736,g737)
    c: Coincident(g737,g738)
    c: Coincident(g738,g739)
    c: Coincident(g739,g740)
    c: Coincident(g740,g741)
    c: Coincident(g741,g742)
    c: Coincident(g742,g743)
    c: Coincident(g743,g744)
    c: Coincident(g744,g745)
    c: Coincident(g745,g746)
    c: Coincident(g746,g747)
    c: Coincident(g747,g748)
    c: Coincident(g748,g749)
    c: Coincident(g749,g750)
    c: Coincident(g750,g751)
    c: Coincident(g751,g752)
    c: Coincident(g752,g753)
    c: Coincident(g753,g754)
    c: Coincident(g754,g755)
    c: Coincident(g755,g756)
    c: Coincident(g756,g757)
    c: Coincident(g757,g758)
    c: Coincident(g760,g761)
    c: Coincident(g761,g762)
    c: Coincident(g762,g763)
    c: Coincident(g763,g764)
    c: Coincident(g765,g766)
    c: Coincident(g766,g767)
    c: Coincident(g767,g768)
    c: Coincident(g769,g770)
    c: Coincident(g770,g771)
    c: Coincident(g772,g773)
    c: Coincident(g773,g774)
    c: Coincident(g774,g775)
    c: Coincident(g775,g776)
    c: Coincident(g776,g777)
    c: Coincident(g777,g778)
    c: Coincident(g778,g779)
    c: Coincident(g779,g780)
    c: Coincident(g780,g781)
    c: Coincident(g781,g782)
    c: Coincident(g782,g783)
    c: Coincident(g783,g784)
    c: Coincident(g784,g785)
    c: Coincident(g785,g786)
    c: Horizontal(g787)
    c: Coincident(g787,g788)
    c: Coincident(g788,g789)
    c: Coincident(g789,g790)
    c: Coincident(g790,g791)
    c: Horizontal(g791)
    c: Coincident(g791,g792)
    c: Coincident(g792,g793)
    c: Horizontal(g793)
    c: Coincident(g793,g794)
    c: Coincident(g794,g795)
    c: Coincident(g795,g796)
    c: Vertical(g796)
    c: Coincident(g796,g797)
    c: Horizontal(g797)
    c: Coincident(g797,g798)
    c: Coincident(g798,g799)
    c: Horizontal(g799)
    c: Coincident(g799,g800)
    c: Coincident(g800,g801)
    c: Coincident(g801,g802)
    c: Coincident(g802,g803)
    c: Horizontal(g803)
    c: Vertical(g804)
    c: Coincident(g804,g805)
    c: Coincident(g805,g806)
    c: Coincident(g806,g807)
    c: Coincident(g807,g808)
    c: Coincident(g808,g809)
    c: Coincident(g809,g810)
    c: Vertical(g810)
    c: Coincident(g810,g811)
    c: Coincident(g811,g812)
    c: Coincident(g812,g813)
    c: Coincident(g813,g814)
    c: Coincident(g814,g815)
    c: Horizontal(g815)
    c: Coincident(g815,g816)
    c: Coincident(g816,g817)
    c: Coincident(g817,g818)
    c: Coincident(g818,g819)
    c: Coincident(g819,g820)
    c: Coincident(g820,g821)
    c: Horizontal(g821)
    c: Coincident(g821,g822)
    c: Vertical(g822)
    c: Coincident(g822,g823)
    c: Coincident(g823,g824)
    c: Coincident(g824,g825)
    c: Horizontal(g825)
    c: Coincident(g825,g826)
    c: Coincident(g826,g827)
    c: Coincident(g827,g828)
    c: Coincident(g828,g829)
    c: Horizontal(g829)
    c: Coincident(g829,g830)
    c: Coincident(g830,g831)
    c: Coincident(g831,g832)
    c: Coincident(g832,g833)
    c: Horizontal(g834)
    c: Coincident(g834,g835)
    c: Coincident(g835,g836)
    c: Horizontal(g836)
    c: Coincident(g836,g837)
    c: Coincident(g837,g838)
    c: Horizontal(g838)
    c: Coincident(g838,g839)
    c: Coincident(g839,g840)
    c: Coincident(g840,g841)
    c: Coincident(g841,g842)
    c: Coincident(g842,g843)
    c: Coincident(g843,g844)
    c: Coincident(g844,g845)
    c: Coincident(g845,g846)
    c: Coincident(g846,g847)
    c: Coincident(g847,g848)
    c: Horizontal(g848)
    c: Coincident(g848,g849)
    c: Coincident(g849,g850)
    c: Coincident(g850,g851)
    c: Coincident(g851,g852)
    c: Coincident(g852,g853)
    c: Coincident(g853,g854)
    c: Coincident(g854,g855)
    c: Coincident(g855,g856)
    c: Coincident(g856,g857)
    c: Coincident(g857,g858)
    c: Horizontal(g858)
    c: Coincident(g858,g859)
    c: Coincident(g859,g860)
    c: Coincident(g860,g861)
    c: Coincident(g861,g862)
    c: Coincident(g862,g863)
    c: Coincident(g863,g864)
    c: Coincident(g786,g865)
    c: Coincident(g865,g866)
    c: Coincident(g866,g787)
    c: Vertical(g866)
    c: Horizontal(g709)
    c: Horizontal(g711)
    c: Horizontal(g715)
    c: Horizontal(g717)
    c: Horizontal(g719)
    c: Horizontal(g722)
    c: Coincident(g718,g867)
    c: Horizontal(g867)
    c: Coincident(g867,g868)
    c: Coincident(g868,g717)
    c: Coincident(g721,g869)
    c: Coincident(g869,g870)
    c: Coincident(g720,g870)
    c: Coincident(g871,g720)
    c: Coincident(g871,g719)
    c: Vertical(g871)
    c: Vertical(g870)
    c: Vertical(g723)
    c: Horizontal(g869)
    c: Coincident(g872,g726)
    c: Coincident(g873,g872)
    c: Coincident(g725,g873)
    c: Horizontal(g873)
    c: Horizontal(g736)
    c: Horizontal(g734)
    c: Horizontal(g732)
    c: Horizontal(g730)
    c: Horizontal(g738)
    c: Horizontal(g740)
    c: Horizontal(g742)
    c: Horizontal(g744)
    c: Horizontal(g746)
    c: Horizontal(g748)
    c: Horizontal(g750)
    c: Horizontal(g752)
    c: Horizontal(g754)
    c: Coincident(g758,g759)
    c: Horizontal(g756)
    c: Horizontal(g758)
    c: Coincident(g874,g759)
    c: Horizontal(g874)
    c: Coincident(g875,g760)
    c: Coincident(g875,g874)
    c: Horizontal(g760)
    c: Vertical(g762)
    c: Coincident(g765,g764)
    c: Vertical(g764)
    c: Vertical(g766)
    c: Vertical(g768)
    c: Coincident(g769,g768)
    c: Vertical(g770)
    c: Coincident(g876,g771)
    c: Coincident(g877,g772)
    c: Coincident(g877,g876)
    c: Vertical(g772)
    c: Vertical(g774)
    c: Vertical(g776)
    c: Vertical(g778)
    c: Vertical(g780)
    c: Vertical(g782)
    c: Vertical(g876)
    c: Horizontal(g773)
    c: Horizontal(g775)
    c: Horizontal(g777)
    c: Horizontal(g779)
    c: Horizontal(g781)
    c: Horizontal(g783)
    c: Horizontal(g785)
    c: Horizontal(g865)
    c: Vertical(g784)
    c: Vertical(g786)
    c: Vertical(g788)
    c: Vertical(g790)
    c: Horizontal(g789)
    c: Vertical(g792)
    c: Vertical(g794)
    c: Horizontal(g795)
    c: Vertical(g798)
    c: Vertical(g800)
    c: Vertical(g802)
    c: Horizontal(g801)
    c: Coincident(g804,g803)
    c: Horizontal(g805)
    c: Horizontal(g807)
    c: Horizontal(g809)
    c: Vertical(g806)
    c: Vertical(g808)
    c: Vertical(g812)
    c: Vertical(g816)
    c: Vertical(g814)
    c: Vertical(g818)
    c: Vertical(g820)
    c: Vertical(g824)
    c: Vertical(g826)
    c: Vertical(g828)
    c: Vertical(g830)
    c: Vertical(g832)
    c: Horizontal(g827)
    c: Horizontal(g823)
    c: Horizontal(g819)
    c: Horizontal(g817)
    c: Horizontal(g831)
    c: Horizontal(g833)
    c: Coincident(g878,g833)
    c: Coincident(g878,g834)
    c: Vertical(g837)
    c: Horizontal(g840)
    c: Horizontal(g842)
    c: Horizontal(g846)
    c: Horizontal(g850)
    c: Horizontal(g852)
    c: Horizontal(g854)
    c: Horizontal(g856)
    c: Horizontal(g860)
    c: Horizontal(g862)
    c: Horizontal(g864)
    c: Horizontal(g844)
    c: Coincident(g864,g879)
    c: Coincident(g879,g880)
    c: Coincident(g880,g881)
    c: Coincident(g881,g882)
    c: Horizontal(g882)
    c: Coincident(g883,g1)
    c: Coincident(g883,g0)
    c: Vertical(g883)
    c: Coincident(g0,g882)
    c: Coincident(g1,g2)
    c: Coincident(g3,g4)
    c: Coincident(g4,g5)
    c: Coincident(g5,g6)
    c: Coincident(g6,g7)
    c: Coincident(g13,g14)
    c: Coincident(g14,g15)
    c: Coincident(g16,g17)
    c: Coincident(g18,g19)
    c: Coincident(g22,g23)
    c: Coincident(g24,g25)
    c: Coincident(g27,g28)
    c: Vertical(g26)
    c: Coincident(g28,g29)
    c: Coincident(g30,g31)
    c: Horizontal(g29)
    c: Coincident(g37,g38)
    c: Coincident(g38,g39)
    c: Coincident(g39,g40)
    c: Coincident(g40,g41)
    c: Coincident(g42,g43)
    c: Coincident(g20,g21)
    c: Coincident(g21,g22)
    c: Coincident(g25,g26)
    c: Coincident(g48,g49)
    c: Coincident(g49,g50)
    c: Coincident(g58,g59)
    c: Horizontal(g59)
    c: Coincident(g61,g62)
    c: Coincident(g64,g65)
    c: Coincident(g65,g66)
    c: Coincident(g66,g67)
    c: Coincident(g68,g69)
    c: Coincident(g70,g71)
    c: Coincident(g72,g73)
    c: Coincident(g74,g75)
    c: Coincident(g86,g87)
    c: Coincident(g87,g88)
    c: Coincident(g92,g93)
    c: Coincident(g94,g95)
    c: Coincident(g96,g97)
    c: Coincident(g51,g52)
    c: Coincident(g62,g63)
    c: Coincident(g76,g77)
    c: Coincident(g77,g78)
    c: Coincident(g82,g83)
    c: Coincident(g83,g84)
FEATURE [Mesh::Feature] tinker
  Placement = pos=(42,-32.19,20) rot=(1,0,0;1.5708rad)
FEATURE [Part::Extrusion] Extrude
  Base = -> Sketch013
  Dir = (0,1,0)
  DirMode = 0
  FaceMakerClass = Part::FaceMakerBullseye
  LengthFwd = 10
  LengthRev = 0
  Solid = true
  Symmetric = false
FEATURE [Part::FeaturePython] Clone  label="scaled0_75"  # Draft clone (typed FeaturePython)
  AttacherType = Attacher::AttachEngine3D
  Fuse = false
  Objects = -> [Extrude]
  Scale = (0.75,0.75,0.75)
FEATURE [Part::FeaturePython] Clone001  label="scaled0_80"  # Draft clone (typed FeaturePython)
  AttacherType = Attacher::AttachEngine3D
  Fuse = false
  Objects = -> [Extrude]
  Scale = (0.8,0.8,0.8)
